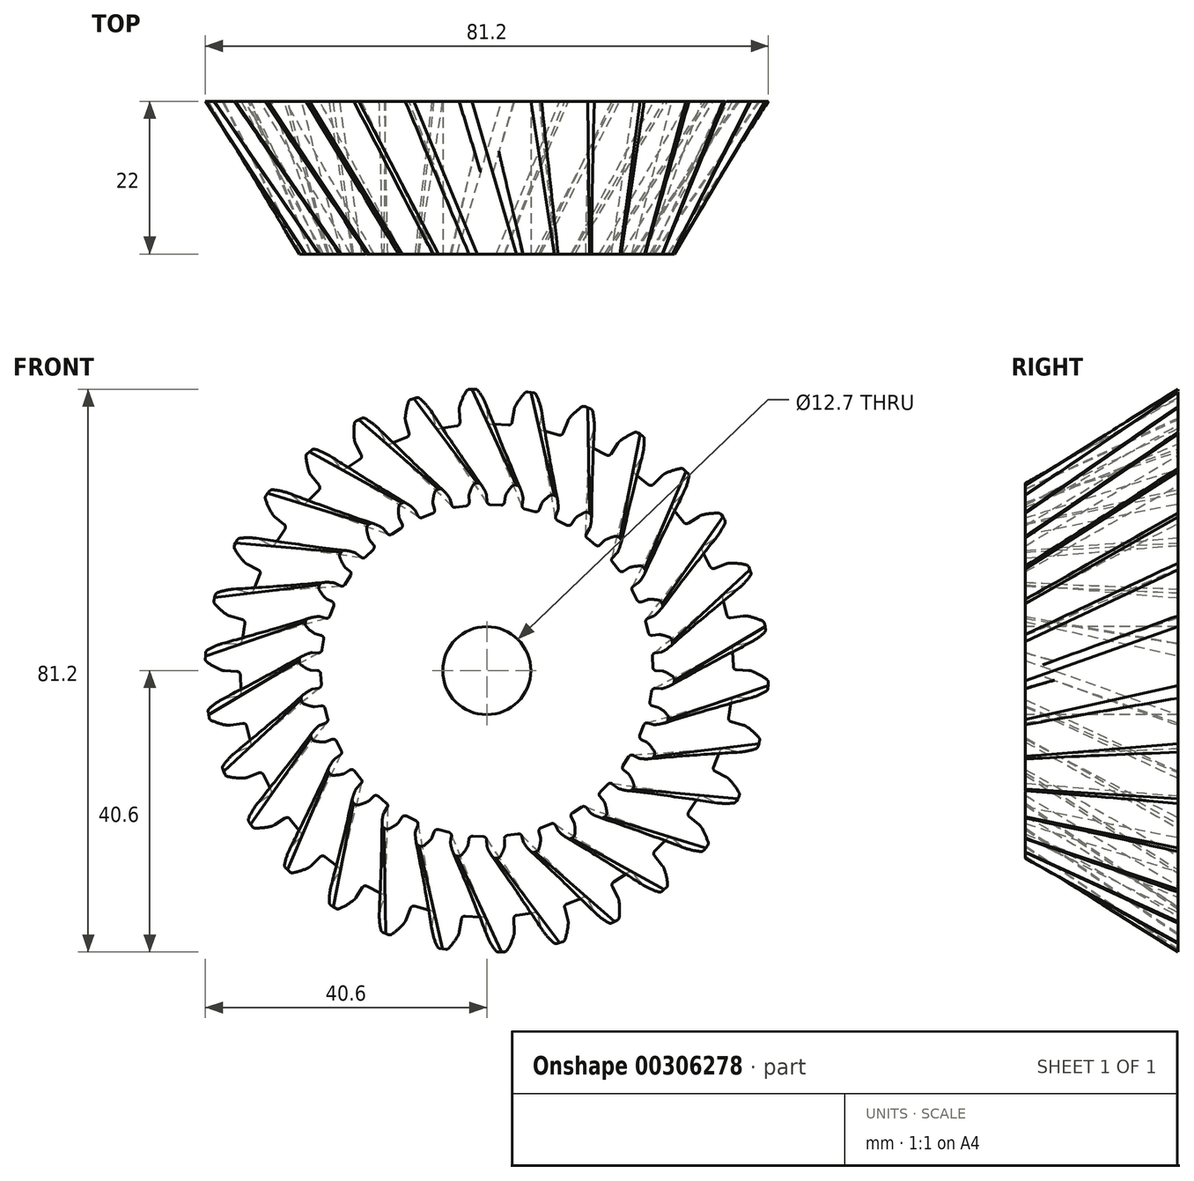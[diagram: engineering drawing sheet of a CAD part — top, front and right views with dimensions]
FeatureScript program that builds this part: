
annotation { "Feature Type Name" : "Feature", "Feature Type Description" : "" }
export const myFeature = defineFeature(function(context is Context, id is Id, definition is map)
    precondition{}
    {
        {
            var Q0;
            Q0=qCreatedBy(makeId("Front.planeOp"),FACE);
            var sketch = newSketch(context, id + "F0", { "sketchPlane" : qUnion([Q0])});
            skArc(sketch, "E0", {"start": v(-0.07, 25.48) * mm, "mid": v(-0.4, 26.19) * mm, "end": v(-0.83, 26.85) * mm});
            skLineSegment(sketch, "E1", {"start": v(-1.24, 27.06) * mm, "end": v(-1.82, 27.06) * mm});
            skLineSegment(sketch, "E2", {"start": v(-0.04, 25.32) * mm, "end": v(0, 24.44) * mm});
            skArc(sketch, "E3.MirrorCS", {"start": v(-2.56, 25.38) * mm, "mid": v(-2.3, 26.1) * mm, "end": v(-1.97, 26.78) * mm});
            skLineSegment(sketch, "E4.MirrorCS", {"start": v(-1.58, 27.03) * mm, "end": v(-0.9, 27.1) * mm});
            skLineSegment(sketch, "E5.MirrorCS", {"start": v(-2.58, 25.21) * mm, "end": v(-2.54, 24.3) * mm});
            skPoint(sketch, "E6.visualSharp", {"position": v(-2.5, 23.57) * mm});
            skArc(sketch, "E6.filletArc", {"start": v(-2.97, 23.78) * mm, "mid": v(-2.65, 23.96) * mm, "end": v(-2.54, 24.3) * mm});
            skPoint(sketch, "E7.visualSharp", {"position": v(0.05, 23.7) * mm});
            skArc(sketch, "E7.filletArc", {"start": v(0, 24.44) * mm, "mid": v(0.16, 24.1) * mm, "end": v(0.5, 23.96) * mm});
            skPoint(sketch, "E8.visualSharp", {"position": v(-2.59, 25.3) * mm});
            skArc(sketch, "E8.filletArc", {"start": v(-2.56, 25.38) * mm, "mid": v(-2.58, 25.3) * mm, "end": v(-2.58, 25.21) * mm});
            skPoint(sketch, "E9.visualSharp", {"position": v(-0.04, 25.4) * mm});
            skArc(sketch, "E9.filletArc", {"start": v(-0.04, 25.32) * mm, "mid": v(-0.05, 25.4) * mm, "end": v(-0.07, 25.48) * mm});
            skPoint(sketch, "E10.visualSharp", {"position": v(-0.99, 27.06) * mm});
            skArc(sketch, "E10.filletArc", {"start": v(-0.83, 26.85) * mm, "mid": v(-1, 27) * mm, "end": v(-1.24, 27.06) * mm});
            skPoint(sketch, "E11.visualSharp", {"position": v(-1.83, 27) * mm});
            skArc(sketch, "E11.filletArc", {"start": v(-1.58, 27.03) * mm, "mid": v(-1.8, 26.95) * mm, "end": v(-1.97, 26.78) * mm});
            skPoint(sketch, "E12.1.0", {"position": v(-6.6, 26.26) * mm});
            skLineSegment(sketch, "E12.1.1", {"start": v(-5.3, 24.75) * mm, "end": v(-5.07, 23.9) * mm});
            skArc(sketch, "E12.1.2", {"start": v(-5.07, 23.9) * mm, "mid": v(-4.85, 23.6) * mm, "end": v(-4.5, 23.54) * mm});
            skPoint(sketch, "E12.1.3", {"position": v(-4.88, 23.2) * mm});
            skArc(sketch, "E12.1.4", {"start": v(-7.78, 24.29) * mm, "mid": v(-7.69, 25.05) * mm, "end": v(-7.5, 25.78) * mm});
            skArc(sketch, "E12.1.5", {"start": v(-7.85, 22.64) * mm, "mid": v(-7.57, 22.88) * mm, "end": v(-7.53, 23.25) * mm});
            skLineSegment(sketch, "E12.1.6", {"start": v(-7.77, 24.12) * mm, "end": v(-7.53, 23.25) * mm});
            skArc(sketch, "E12.1.7", {"start": v(-5.37, 24.9) * mm, "mid": v(-5.84, 25.53) * mm, "end": v(-6.4, 26.09) * mm});
            skPoint(sketch, "E12.1.8", {"position": v(-7.34, 22.54) * mm});
            skPoint(sketch, "E12.1.9", {"position": v(-5.32, 24.83) * mm});
            skPoint(sketch, "E12.1.10", {"position": v(-7.79, 24.2) * mm});
            skPoint(sketch, "E12.1.11", {"position": v(-7.4, 26.03) * mm});
            skArc(sketch, "E12.1.12", {"start": v(-7.17, 26.11) * mm, "mid": v(-7.37, 25.99) * mm, "end": v(-7.5, 25.78) * mm});
            skArc(sketch, "E12.1.13", {"start": v(-6.4, 26.09) * mm, "mid": v(-6.6, 26.2) * mm, "end": v(-6.84, 26.2) * mm});
            skArc(sketch, "E12.1.14", {"start": v(-5.3, 24.75) * mm, "mid": v(-5.33, 24.83) * mm, "end": v(-5.37, 24.9) * mm});
            skArc(sketch, "E12.1.15", {"start": v(-7.78, 24.29) * mm, "mid": v(-7.78, 24.2) * mm, "end": v(-7.77, 24.12) * mm});
            skLineSegment(sketch, "E12.1.16", {"start": v(-6.84, 26.2) * mm, "end": v(-7.4, 26.09) * mm});
            skLineSegment(sketch, "E12.1.17", {"start": v(-7.17, 26.11) * mm, "end": v(-6.52, 26.32) * mm});
            skPoint(sketch, "E12.2.0", {"position": v(-11.9, 24.31) * mm});
            skLineSegment(sketch, "E12.2.1", {"start": v(-10.33, 23.11) * mm, "end": v(-9.93, 22.33) * mm});
            skArc(sketch, "E12.2.2", {"start": v(-9.93, 22.33) * mm, "mid": v(-9.66, 22.08) * mm, "end": v(-9.29, 22.09) * mm});
            skPoint(sketch, "E12.2.3", {"position": v(-9.6, 21.67) * mm});
            skArc(sketch, "E12.2.4", {"start": v(-12.66, 22.14) * mm, "mid": v(-12.72, 22.9) * mm, "end": v(-12.7, 23.66) * mm});
            skArc(sketch, "E12.2.5", {"start": v(-12.39, 20.51) * mm, "mid": v(-12.17, 20.8) * mm, "end": v(-12.2, 21.17) * mm});
            skLineSegment(sketch, "E12.2.6", {"start": v(-12.61, 21.98) * mm, "end": v(-12.2, 21.17) * mm});
            skArc(sketch, "E12.2.7", {"start": v(-10.43, 23.24) * mm, "mid": v(-11.02, 23.76) * mm, "end": v(-11.68, 24.19) * mm});
            skPoint(sketch, "E12.2.8", {"position": v(-11.87, 20.52) * mm});
            skPoint(sketch, "E12.2.9", {"position": v(-10.37, 23.18) * mm});
            skPoint(sketch, "E12.2.10", {"position": v(-12.65, 22.05) * mm});
            skPoint(sketch, "E12.2.11", {"position": v(-12.66, 23.92) * mm});
            skArc(sketch, "E12.2.12", {"start": v(-12.44, 24.05) * mm, "mid": v(-12.61, 23.89) * mm, "end": v(-12.7, 23.66) * mm});
            skArc(sketch, "E12.2.13", {"start": v(-11.68, 24.19) * mm, "mid": v(-11.9, 24.26) * mm, "end": v(-12.14, 24.21) * mm});
            skArc(sketch, "E12.2.14", {"start": v(-10.33, 23.11) * mm, "mid": v(-10.37, 23.18) * mm, "end": v(-10.43, 23.24) * mm});
            skArc(sketch, "E12.2.15", {"start": v(-12.66, 22.14) * mm, "mid": v(-12.65, 22.06) * mm, "end": v(-12.61, 21.98) * mm});
            skLineSegment(sketch, "E12.2.16", {"start": v(-12.14, 24.21) * mm, "end": v(-12.67, 23.98) * mm});
            skLineSegment(sketch, "E12.2.17", {"start": v(-12.44, 24.05) * mm, "end": v(-11.85, 24.4) * mm});
            skPoint(sketch, "E12.3.0", {"position": v(-16.7, 21.3) * mm});
            skLineSegment(sketch, "E12.3.1", {"start": v(-14.91, 20.46) * mm, "end": v(-14.36, 19.77) * mm});
            skArc(sketch, "E12.3.2", {"start": v(-14.36, 19.77) * mm, "mid": v(-14.04, 19.6) * mm, "end": v(-13.68, 19.67) * mm});
            skPoint(sketch, "E12.3.3", {"position": v(-13.9, 19.2) * mm});
            skArc(sketch, "E12.3.4", {"start": v(-17, 19.02) * mm, "mid": v(-17.2, 19.75) * mm, "end": v(-17.33, 20.5) * mm});
            skArc(sketch, "E12.3.5", {"start": v(-16.38, 17.49) * mm, "mid": v(-16.23, 17.82) * mm, "end": v(-16.34, 18.17) * mm});
            skLineSegment(sketch, "E12.3.6", {"start": v(-16.9, 18.88) * mm, "end": v(-16.34, 18.17) * mm});
            skArc(sketch, "E12.3.7", {"start": v(-15.03, 20.57) * mm, "mid": v(-15.72, 20.94) * mm, "end": v(-16.45, 21.23) * mm});
            skPoint(sketch, "E12.3.8", {"position": v(-15.88, 17.6) * mm});
            skPoint(sketch, "E12.3.9", {"position": v(-14.96, 20.52) * mm});
            skPoint(sketch, "E12.3.10", {"position": v(-16.96, 18.94) * mm});
            skPoint(sketch, "E12.3.11", {"position": v(-17.36, 20.77) * mm});
            skArc(sketch, "E12.3.12", {"start": v(-17.17, 20.94) * mm, "mid": v(-17.3, 20.74) * mm, "end": v(-17.33, 20.5) * mm});
            skArc(sketch, "E12.3.13", {"start": v(-16.45, 21.23) * mm, "mid": v(-16.69, 21.25) * mm, "end": v(-16.9, 21.16) * mm});
            skArc(sketch, "E12.3.14", {"start": v(-14.91, 20.46) * mm, "mid": v(-14.97, 20.52) * mm, "end": v(-15.03, 20.57) * mm});
            skArc(sketch, "E12.3.15", {"start": v(-17, 19.02) * mm, "mid": v(-16.96, 18.95) * mm, "end": v(-16.9, 18.88) * mm});
            skLineSegment(sketch, "E12.3.16", {"start": v(-16.9, 21.16) * mm, "end": v(-17.38, 20.82) * mm});
            skLineSegment(sketch, "E12.3.17", {"start": v(-17.17, 20.94) * mm, "end": v(-16.66, 21.4) * mm});
            skPoint(sketch, "E12.4.0", {"position": v(-20.77, 17.37) * mm});
            skLineSegment(sketch, "E12.4.1", {"start": v(-18.84, 16.91) * mm, "end": v(-18.15, 16.36) * mm});
            skArc(sketch, "E12.4.2", {"start": v(-18.15, 16.36) * mm, "mid": v(-17.8, 16.25) * mm, "end": v(-17.47, 16.4) * mm});
            skPoint(sketch, "E12.4.3", {"position": v(-17.58, 15.9) * mm});
            skArc(sketch, "E12.4.4", {"start": v(-20.57, 15.08) * mm, "mid": v(-20.94, 15.75) * mm, "end": v(-21.22, 16.45) * mm});
            skArc(sketch, "E12.4.5", {"start": v(-19.66, 13.7) * mm, "mid": v(-19.58, 14.06) * mm, "end": v(-19.76, 14.38) * mm});
            skLineSegment(sketch, "E12.4.6", {"start": v(-20.46, 14.95) * mm, "end": v(-19.76, 14.38) * mm});
            skArc(sketch, "E12.4.7", {"start": v(-18.98, 17) * mm, "mid": v(-19.73, 17.22) * mm, "end": v(-20.5, 17.35) * mm});
            skPoint(sketch, "E12.4.8", {"position": v(-19.2, 13.92) * mm});
            skPoint(sketch, "E12.4.9", {"position": v(-18.9, 16.96) * mm});
            skPoint(sketch, "E12.4.10", {"position": v(-20.53, 15) * mm});
            skPoint(sketch, "E12.4.11", {"position": v(-21.3, 16.7) * mm});
            skArc(sketch, "E12.4.12", {"start": v(-21.15, 16.91) * mm, "mid": v(-21.24, 16.7) * mm, "end": v(-21.22, 16.45) * mm});
            skArc(sketch, "E12.4.13", {"start": v(-20.5, 17.35) * mm, "mid": v(-20.74, 17.32) * mm, "end": v(-20.94, 17.18) * mm});
            skArc(sketch, "E12.4.14", {"start": v(-18.84, 16.91) * mm, "mid": v(-18.9, 16.96) * mm, "end": v(-18.98, 17) * mm});
            skArc(sketch, "E12.4.15", {"start": v(-20.57, 15.08) * mm, "mid": v(-20.52, 15) * mm, "end": v(-20.46, 14.95) * mm});
            skLineSegment(sketch, "E12.4.16", {"start": v(-20.94, 17.18) * mm, "end": v(-21.33, 16.75) * mm});
            skLineSegment(sketch, "E12.4.17", {"start": v(-21.15, 16.91) * mm, "end": v(-20.75, 17.46) * mm});
            skPoint(sketch, "E12.5.0", {"position": v(-23.93, 12.67) * mm});
            skLineSegment(sketch, "E12.5.1", {"start": v(-21.94, 12.62) * mm, "end": v(-21.16, 12.23) * mm});
            skArc(sketch, "E12.5.2", {"start": v(-21.16, 12.23) * mm, "mid": v(-20.8, 12.19) * mm, "end": v(-20.5, 12.4) * mm});
            skPoint(sketch, "E12.5.3", {"position": v(-20.5, 11.9) * mm});
            skArc(sketch, "E12.5.4", {"start": v(-23.26, 10.47) * mm, "mid": v(-23.75, 11.05) * mm, "end": v(-24.18, 11.68) * mm});
            skArc(sketch, "E12.5.5", {"start": v(-22.08, 9.31) * mm, "mid": v(-22.07, 9.68) * mm, "end": v(-22.32, 9.96) * mm});
            skLineSegment(sketch, "E12.5.6", {"start": v(-23.12, 10.37) * mm, "end": v(-22.32, 9.96) * mm});
            skArc(sketch, "E12.5.7", {"start": v(-22.1, 12.68) * mm, "mid": v(-22.88, 12.74) * mm, "end": v(-23.66, 12.7) * mm});
            skPoint(sketch, "E12.5.8", {"position": v(-21.67, 9.62) * mm});
            skPoint(sketch, "E12.5.9", {"position": v(-22.02, 12.66) * mm});
            skPoint(sketch, "E12.5.10", {"position": v(-23.2, 10.4) * mm});
            skPoint(sketch, "E12.5.11", {"position": v(-24.3, 11.91) * mm});
            skArc(sketch, "E12.5.12", {"start": v(-24.2, 12.14) * mm, "mid": v(-24.24, 11.91) * mm, "end": v(-24.18, 11.68) * mm});
            skArc(sketch, "E12.5.13", {"start": v(-23.66, 12.7) * mm, "mid": v(-23.89, 12.63) * mm, "end": v(-24.05, 12.45) * mm});
            skArc(sketch, "E12.5.14", {"start": v(-21.94, 12.62) * mm, "mid": v(-22.02, 12.66) * mm, "end": v(-22.1, 12.68) * mm});
            skArc(sketch, "E12.5.15", {"start": v(-23.26, 10.47) * mm, "mid": v(-23.2, 10.41) * mm, "end": v(-23.12, 10.37) * mm});
            skLineSegment(sketch, "E12.5.16", {"start": v(-24.05, 12.45) * mm, "end": v(-24.34, 11.95) * mm});
            skLineSegment(sketch, "E12.5.17", {"start": v(-24.2, 12.14) * mm, "end": v(-23.93, 12.77) * mm});
            skPoint(sketch, "E12.6.0", {"position": v(-26.04, 7.42) * mm});
            skLineSegment(sketch, "E12.6.1", {"start": v(-24.09, 7.79) * mm, "end": v(-23.24, 7.56) * mm});
            skArc(sketch, "E12.6.2", {"start": v(-23.24, 7.56) * mm, "mid": v(-22.87, 7.6) * mm, "end": v(-22.63, 7.88) * mm});
            skPoint(sketch, "E12.6.3", {"position": v(-22.53, 7.37) * mm});
            skArc(sketch, "E12.6.4", {"start": v(-24.93, 5.4) * mm, "mid": v(-25.53, 5.87) * mm, "end": v(-26.08, 6.4) * mm});
            skArc(sketch, "E12.6.5", {"start": v(-23.53, 4.52) * mm, "mid": v(-23.6, 4.88) * mm, "end": v(-23.9, 5.1) * mm});
            skLineSegment(sketch, "E12.6.6", {"start": v(-24.77, 5.33) * mm, "end": v(-23.9, 5.1) * mm});
            skArc(sketch, "E12.6.7", {"start": v(-24.25, 7.8) * mm, "mid": v(-25.03, 7.7) * mm, "end": v(-25.79, 7.5) * mm});
            skPoint(sketch, "E12.6.8", {"position": v(-23.2, 4.9) * mm});
            skPoint(sketch, "E12.6.9", {"position": v(-24.17, 7.8) * mm});
            skPoint(sketch, "E12.6.10", {"position": v(-24.86, 5.36) * mm});
            skPoint(sketch, "E12.6.11", {"position": v(-26.25, 6.6) * mm});
            skArc(sketch, "E12.6.12", {"start": v(-26.2, 6.85) * mm, "mid": v(-26.2, 6.6) * mm, "end": v(-26.08, 6.4) * mm});
            skArc(sketch, "E12.6.13", {"start": v(-25.79, 7.5) * mm, "mid": v(-26, 7.38) * mm, "end": v(-26.11, 7.18) * mm});
            skArc(sketch, "E12.6.14", {"start": v(-24.09, 7.79) * mm, "mid": v(-24.17, 7.8) * mm, "end": v(-24.25, 7.8) * mm});
            skArc(sketch, "E12.6.15", {"start": v(-24.93, 5.4) * mm, "mid": v(-24.85, 5.36) * mm, "end": v(-24.77, 5.33) * mm});
            skLineSegment(sketch, "E12.6.16", {"start": v(-26.11, 7.18) * mm, "end": v(-26.3, 6.63) * mm});
            skLineSegment(sketch, "E12.6.17", {"start": v(-26.2, 6.85) * mm, "end": v(-26.06, 7.51) * mm});
            skPoint(sketch, "E12.7.0", {"position": v(-27.01, 1.85) * mm});
            skLineSegment(sketch, "E12.7.1", {"start": v(-25.18, 2.6) * mm, "end": v(-24.3, 2.56) * mm});
            skArc(sketch, "E12.7.2", {"start": v(-24.3, 2.56) * mm, "mid": v(-23.95, 2.68) * mm, "end": v(-23.77, 3) * mm});
            skPoint(sketch, "E12.7.3", {"position": v(-23.57, 2.52) * mm});
            skArc(sketch, "E12.7.4", {"start": v(-25.5, 0.1) * mm, "mid": v(-26.2, 0.43) * mm, "end": v(-26.84, 0.84) * mm});
            skArc(sketch, "E12.7.5", {"start": v(-23.96, -0.47) * mm, "mid": v(-24.1, -0.13) * mm, "end": v(-24.44, 0.02) * mm});
            skLineSegment(sketch, "E12.7.6", {"start": v(-25.34, 0.07) * mm, "end": v(-24.44, 0.02) * mm});
            skArc(sketch, "E12.7.7", {"start": v(-25.35, 2.6) * mm, "mid": v(-26.08, 2.33) * mm, "end": v(-26.79, 1.98) * mm});
            skPoint(sketch, "E12.7.8", {"position": v(-23.7, -0.02) * mm});
            skPoint(sketch, "E12.7.9", {"position": v(-25.26, 2.61) * mm});
            skPoint(sketch, "E12.7.10", {"position": v(-25.43, 0.07) * mm});
            skPoint(sketch, "E12.7.11", {"position": v(-27.05, 1) * mm});
            skArc(sketch, "E12.7.12", {"start": v(-27.05, 1.25) * mm, "mid": v(-27, 1.02) * mm, "end": v(-26.84, 0.84) * mm});
            skArc(sketch, "E12.7.13", {"start": v(-26.79, 1.98) * mm, "mid": v(-26.96, 1.82) * mm, "end": v(-27.04, 1.6) * mm});
            skArc(sketch, "E12.7.14", {"start": v(-25.18, 2.6) * mm, "mid": v(-25.26, 2.6) * mm, "end": v(-25.35, 2.6) * mm});
            skArc(sketch, "E12.7.15", {"start": v(-25.5, 0.1) * mm, "mid": v(-25.43, 0.08) * mm, "end": v(-25.34, 0.07) * mm});
            skLineSegment(sketch, "E12.7.16", {"start": v(-27.04, 1.6) * mm, "end": v(-27.1, 1.02) * mm});
            skLineSegment(sketch, "E12.7.17", {"start": v(-27.05, 1.25) * mm, "end": v(-27.05, 1.93) * mm});
            skPoint(sketch, "E12.8.0", {"position": v(-26.8, -3.81) * mm});
            skLineSegment(sketch, "E12.8.1", {"start": v(-25.17, -2.68) * mm, "end": v(-24.3, -2.55) * mm});
            skArc(sketch, "E12.8.2", {"start": v(-24.3, -2.55) * mm, "mid": v(-23.99, -2.36) * mm, "end": v(-23.88, -2) * mm});
            skPoint(sketch, "E12.8.3", {"position": v(-23.58, -2.43) * mm});
            skArc(sketch, "E12.8.4", {"start": v(-24.97, -5.2) * mm, "mid": v(-25.71, -5.03) * mm, "end": v(-26.43, -4.76) * mm});
            skArc(sketch, "E12.8.5", {"start": v(-23.34, -5.44) * mm, "mid": v(-23.55, -5.14) * mm, "end": v(-23.9, -5.06) * mm});
            skLineSegment(sketch, "E12.8.6", {"start": v(-24.8, -5.2) * mm, "end": v(-23.9, -5.06) * mm});
            skArc(sketch, "E12.8.7", {"start": v(-25.33, -2.74) * mm, "mid": v(-26, -3.14) * mm, "end": v(-26.61, -3.63) * mm});
            skPoint(sketch, "E12.8.8", {"position": v(-23.18, -4.95) * mm});
            skPoint(sketch, "E12.8.9", {"position": v(-25.25, -2.7) * mm});
            skPoint(sketch, "E12.8.10", {"position": v(-24.88, -5.22) * mm});
            skPoint(sketch, "E12.8.11", {"position": v(-26.67, -4.65) * mm});
            skArc(sketch, "E12.8.12", {"start": v(-26.72, -4.4) * mm, "mid": v(-26.62, -4.61) * mm, "end": v(-26.43, -4.76) * mm});
            skArc(sketch, "E12.8.13", {"start": v(-26.61, -3.63) * mm, "mid": v(-26.75, -3.83) * mm, "end": v(-26.78, -4.06) * mm});
            skArc(sketch, "E12.8.14", {"start": v(-25.17, -2.68) * mm, "mid": v(-25.25, -2.7) * mm, "end": v(-25.33, -2.74) * mm});
            skArc(sketch, "E12.8.15", {"start": v(-24.97, -5.2) * mm, "mid": v(-24.89, -5.21) * mm, "end": v(-24.8, -5.2) * mm});
            skLineSegment(sketch, "E12.8.16", {"start": v(-26.78, -4.06) * mm, "end": v(-26.72, -4.64) * mm});
            skLineSegment(sketch, "E12.8.17", {"start": v(-26.72, -4.4) * mm, "end": v(-26.86, -3.74) * mm});
            skPoint(sketch, "E12.9.0", {"position": v(-25.43, -9.3) * mm});
            skLineSegment(sketch, "E12.9.1", {"start": v(-24.06, -7.86) * mm, "end": v(-23.24, -7.54) * mm});
            skArc(sketch, "E12.9.2", {"start": v(-23.24, -7.54) * mm, "mid": v(-22.97, -7.3) * mm, "end": v(-22.94, -6.93) * mm});
            skPoint(sketch, "E12.9.3", {"position": v(-22.56, -7.28) * mm});
            skArc(sketch, "E12.9.4", {"start": v(-23.34, -10.28) * mm, "mid": v(-24.1, -10.26) * mm, "end": v(-24.86, -10.15) * mm});
            skArc(sketch, "E12.9.5", {"start": v(-21.7, -10.17) * mm, "mid": v(-21.97, -9.92) * mm, "end": v(-22.33, -9.92) * mm});
            skLineSegment(sketch, "E12.9.6", {"start": v(-23.18, -10.25) * mm, "end": v(-22.33, -9.92) * mm});
            skArc(sketch, "E12.9.7", {"start": v(-24.2, -7.94) * mm, "mid": v(-24.78, -8.48) * mm, "end": v(-25.28, -9.08) * mm});
            skPoint(sketch, "E12.9.8", {"position": v(-21.65, -9.66) * mm});
            skPoint(sketch, "E12.9.9", {"position": v(-24.14, -7.89) * mm});
            skPoint(sketch, "E12.9.10", {"position": v(-23.26, -10.28) * mm});
            skPoint(sketch, "E12.9.11", {"position": v(-25.12, -10.1) * mm});
            skArc(sketch, "E12.9.12", {"start": v(-25.22, -9.86) * mm, "mid": v(-25.07, -10.05) * mm, "end": v(-24.86, -10.15) * mm});
            skArc(sketch, "E12.9.13", {"start": v(-25.28, -9.08) * mm, "mid": v(-25.37, -9.3) * mm, "end": v(-25.35, -9.54) * mm});
            skArc(sketch, "E12.9.14", {"start": v(-24.06, -7.86) * mm, "mid": v(-24.14, -7.9) * mm, "end": v(-24.2, -7.94) * mm});
            skArc(sketch, "E12.9.15", {"start": v(-23.34, -10.28) * mm, "mid": v(-23.26, -10.27) * mm, "end": v(-23.18, -10.25) * mm});
            skLineSegment(sketch, "E12.9.16", {"start": v(-25.35, -9.54) * mm, "end": v(-25.17, -10.1) * mm});
            skLineSegment(sketch, "E12.9.17", {"start": v(-25.22, -9.86) * mm, "end": v(-25.5, -9.24) * mm});
            skPoint(sketch, "E12.10.0", {"position": v(-22.94, -14.38) * mm});
            skLineSegment(sketch, "E12.10.1", {"start": v(-21.9, -12.7) * mm, "end": v(-21.17, -12.21) * mm});
            skArc(sketch, "E12.10.2", {"start": v(-21.17, -12.21) * mm, "mid": v(-20.95, -11.91) * mm, "end": v(-21, -11.55) * mm});
            skPoint(sketch, "E12.10.3", {"position": v(-20.55, -11.81) * mm});
            skArc(sketch, "E12.10.4", {"start": v(-20.7, -14.9) * mm, "mid": v(-21.45, -15.05) * mm, "end": v(-22.2, -15.1) * mm});
            skArc(sketch, "E12.10.5", {"start": v(-19.1, -14.46) * mm, "mid": v(-19.42, -14.27) * mm, "end": v(-19.78, -14.35) * mm});
            skLineSegment(sketch, "E12.10.6", {"start": v(-20.54, -14.84) * mm, "end": v(-19.78, -14.35) * mm});
            skArc(sketch, "E12.10.7", {"start": v(-22.03, -12.8) * mm, "mid": v(-22.47, -13.45) * mm, "end": v(-22.83, -14.14) * mm});
            skPoint(sketch, "E12.10.8", {"position": v(-19.17, -13.95) * mm});
            skPoint(sketch, "E12.10.9", {"position": v(-21.97, -12.74) * mm});
            skPoint(sketch, "E12.10.10", {"position": v(-20.61, -14.89) * mm});
            skPoint(sketch, "E12.10.11", {"position": v(-22.47, -15.1) * mm});
            skArc(sketch, "E12.10.12", {"start": v(-22.62, -14.89) * mm, "mid": v(-22.44, -15.04) * mm, "end": v(-22.2, -15.1) * mm});
            skArc(sketch, "E12.10.13", {"start": v(-22.83, -14.14) * mm, "mid": v(-22.88, -14.37) * mm, "end": v(-22.81, -14.6) * mm});
            skArc(sketch, "E12.10.14", {"start": v(-21.9, -12.7) * mm, "mid": v(-21.97, -12.74) * mm, "end": v(-22.03, -12.8) * mm});
            skArc(sketch, "E12.10.15", {"start": v(-20.7, -14.9) * mm, "mid": v(-20.62, -14.88) * mm, "end": v(-20.54, -14.84) * mm});
            skLineSegment(sketch, "E12.10.16", {"start": v(-22.81, -14.6) * mm, "end": v(-22.52, -15.1) * mm});
            skLineSegment(sketch, "E12.10.17", {"start": v(-22.62, -14.89) * mm, "end": v(-23.02, -14.34) * mm});
            skPoint(sketch, "E12.11.0", {"position": v(-19.44, -18.84) * mm});
            skLineSegment(sketch, "E12.11.1", {"start": v(-18.79, -16.97) * mm, "end": v(-18.17, -16.34) * mm});
            skArc(sketch, "E12.11.2", {"start": v(-18.17, -16.34) * mm, "mid": v(-18.02, -16) * mm, "end": v(-18.14, -15.66) * mm});
            skPoint(sketch, "E12.11.3", {"position": v(-17.65, -15.83) * mm});
            skArc(sketch, "E12.11.4", {"start": v(-17.14, -18.89) * mm, "mid": v(-17.85, -19.18) * mm, "end": v(-18.58, -19.38) * mm});
            skArc(sketch, "E12.11.5", {"start": v(-15.68, -18.12) * mm, "mid": v(-16.03, -18) * mm, "end": v(-16.37, -18.15) * mm});
            skLineSegment(sketch, "E12.11.6", {"start": v(-17, -18.79) * mm, "end": v(-16.37, -18.15) * mm});
            skArc(sketch, "E12.11.7", {"start": v(-18.88, -17.1) * mm, "mid": v(-19.19, -17.83) * mm, "end": v(-19.4, -18.58) * mm});
            skPoint(sketch, "E12.11.8", {"position": v(-15.85, -17.63) * mm});
            skPoint(sketch, "E12.11.9", {"position": v(-18.85, -17.03) * mm});
            skPoint(sketch, "E12.11.10", {"position": v(-17.07, -18.85) * mm});
            skPoint(sketch, "E12.11.11", {"position": v(-18.84, -19.43) * mm});
            skArc(sketch, "E12.11.12", {"start": v(-19.03, -19.26) * mm, "mid": v(-18.82, -19.38) * mm, "end": v(-18.58, -19.38) * mm});
            skArc(sketch, "E12.11.13", {"start": v(-19.4, -18.58) * mm, "mid": v(-19.39, -18.82) * mm, "end": v(-19.28, -19.03) * mm});
            skArc(sketch, "E12.11.14", {"start": v(-18.79, -16.97) * mm, "mid": v(-18.84, -17.03) * mm, "end": v(-18.88, -17.1) * mm});
            skArc(sketch, "E12.11.15", {"start": v(-17.14, -18.89) * mm, "mid": v(-17.07, -18.84) * mm, "end": v(-17, -18.79) * mm});
            skLineSegment(sketch, "E12.11.16", {"start": v(-19.28, -19.03) * mm, "end": v(-18.89, -19.46) * mm});
            skLineSegment(sketch, "E12.11.17", {"start": v(-19.03, -19.26) * mm, "end": v(-19.53, -18.8) * mm});
            skPoint(sketch, "E12.12.0", {"position": v(-15.1, -22.47) * mm});
            skLineSegment(sketch, "E12.12.1", {"start": v(-14.85, -20.5) * mm, "end": v(-14.37, -19.76) * mm});
            skArc(sketch, "E12.12.2", {"start": v(-14.37, -19.76) * mm, "mid": v(-14.3, -19.4) * mm, "end": v(-14.48, -19.09) * mm});
            skPoint(sketch, "E12.12.3", {"position": v(-13.97, -19.15) * mm});
            skArc(sketch, "E12.12.4", {"start": v(-12.84, -22.04) * mm, "mid": v(-13.47, -22.47) * mm, "end": v(-14.15, -22.82) * mm});
            skArc(sketch, "E12.12.5", {"start": v(-11.57, -20.98) * mm, "mid": v(-11.94, -20.94) * mm, "end": v(-12.24, -21.16) * mm});
            skLineSegment(sketch, "E12.12.6", {"start": v(-12.73, -21.91) * mm, "end": v(-12.24, -21.16) * mm});
            skArc(sketch, "E12.12.7", {"start": v(-14.92, -20.65) * mm, "mid": v(-15.06, -21.42) * mm, "end": v(-15.1, -22.2) * mm});
            skPoint(sketch, "E12.12.8", {"position": v(-11.84, -20.54) * mm});
            skPoint(sketch, "E12.12.9", {"position": v(-14.9, -20.57) * mm});
            skPoint(sketch, "E12.12.10", {"position": v(-12.77, -21.98) * mm});
            skPoint(sketch, "E12.12.11", {"position": v(-14.39, -22.93) * mm});
            skArc(sketch, "E12.12.12", {"start": v(-14.6, -22.8) * mm, "mid": v(-14.38, -22.87) * mm, "end": v(-14.15, -22.82) * mm});
            skArc(sketch, "E12.12.13", {"start": v(-15.1, -22.2) * mm, "mid": v(-15.05, -22.44) * mm, "end": v(-14.9, -22.62) * mm});
            skArc(sketch, "E12.12.14", {"start": v(-14.85, -20.5) * mm, "mid": v(-14.89, -20.58) * mm, "end": v(-14.92, -20.65) * mm});
            skArc(sketch, "E12.12.15", {"start": v(-12.84, -22.04) * mm, "mid": v(-12.78, -21.98) * mm, "end": v(-12.73, -21.91) * mm});
            skLineSegment(sketch, "E12.12.16", {"start": v(-14.9, -22.62) * mm, "end": v(-14.43, -22.96) * mm});
            skLineSegment(sketch, "E12.12.17", {"start": v(-14.6, -22.8) * mm, "end": v(-15.2, -22.46) * mm});
            skPoint(sketch, "E12.13.0", {"position": v(-10.1, -25.12) * mm});
            skLineSegment(sketch, "E12.13.1", {"start": v(-10.26, -23.14) * mm, "end": v(-9.95, -22.32) * mm});
            skArc(sketch, "E12.13.2", {"start": v(-9.95, -22.32) * mm, "mid": v(-9.95, -21.95) * mm, "end": v(-10.2, -21.68) * mm});
            skPoint(sketch, "E12.13.3", {"position": v(-9.68, -21.64) * mm});
            skArc(sketch, "E12.13.4", {"start": v(-7.98, -24.23) * mm, "mid": v(-8.5, -24.78) * mm, "end": v(-9.1, -25.27) * mm});
            skArc(sketch, "E12.13.5", {"start": v(-6.96, -22.93) * mm, "mid": v(-7.32, -22.96) * mm, "end": v(-7.57, -23.24) * mm});
            skLineSegment(sketch, "E12.13.6", {"start": v(-7.9, -24.08) * mm, "end": v(-7.57, -23.24) * mm});
            skArc(sketch, "E12.13.7", {"start": v(-10.3, -23.3) * mm, "mid": v(-10.28, -24.09) * mm, "end": v(-10.16, -24.86) * mm});
            skPoint(sketch, "E12.13.8", {"position": v(-7.3, -22.55) * mm});
            skPoint(sketch, "E12.13.9", {"position": v(-10.3, -23.22) * mm});
            skPoint(sketch, "E12.13.10", {"position": v(-7.92, -24.16) * mm});
            skPoint(sketch, "E12.13.11", {"position": v(-9.3, -25.42) * mm});
            skArc(sketch, "E12.13.12", {"start": v(-9.55, -25.34) * mm, "mid": v(-9.31, -25.36) * mm, "end": v(-9.1, -25.27) * mm});
            skArc(sketch, "E12.13.13", {"start": v(-10.16, -24.86) * mm, "mid": v(-10.06, -25.08) * mm, "end": v(-9.87, -25.22) * mm});
            skArc(sketch, "E12.13.14", {"start": v(-10.26, -23.14) * mm, "mid": v(-10.29, -23.22) * mm, "end": v(-10.3, -23.3) * mm});
            skArc(sketch, "E12.13.15", {"start": v(-7.98, -24.23) * mm, "mid": v(-7.93, -24.16) * mm, "end": v(-7.9, -24.08) * mm});
            skLineSegment(sketch, "E12.13.16", {"start": v(-9.87, -25.22) * mm, "end": v(-9.34, -25.46) * mm});
            skLineSegment(sketch, "E12.13.17", {"start": v(-9.55, -25.34) * mm, "end": v(-10.2, -25.13) * mm});
            skPoint(sketch, "E12.14.0", {"position": v(-4.66, -26.67) * mm});
            skLineSegment(sketch, "E12.14.1", {"start": v(-5.23, -24.77) * mm, "end": v(-5.09, -23.9) * mm});
            skArc(sketch, "E12.14.2", {"start": v(-5.09, -23.9) * mm, "mid": v(-5.17, -23.54) * mm, "end": v(-5.47, -23.33) * mm});
            skPoint(sketch, "E12.14.3", {"position": v(-4.97, -23.18) * mm});
            skArc(sketch, "E12.14.4", {"start": v(-2.77, -25.36) * mm, "mid": v(-3.17, -26) * mm, "end": v(-3.64, -26.6) * mm});
            skArc(sketch, "E12.14.5", {"start": v(-2.04, -23.88) * mm, "mid": v(-2.39, -23.98) * mm, "end": v(-2.57, -24.3) * mm});
            skLineSegment(sketch, "E12.14.6", {"start": v(-2.71, -25.2) * mm, "end": v(-2.57, -24.3) * mm});
            skArc(sketch, "E12.14.7", {"start": v(-5.23, -24.94) * mm, "mid": v(-5.04, -25.7) * mm, "end": v(-4.77, -26.43) * mm});
            skPoint(sketch, "E12.14.8", {"position": v(-2.46, -23.58) * mm});
            skPoint(sketch, "E12.14.9", {"position": v(-5.24, -24.85) * mm});
            skPoint(sketch, "E12.14.10", {"position": v(-2.73, -25.28) * mm});
            skPoint(sketch, "E12.14.11", {"position": v(-3.82, -26.8) * mm});
            skArc(sketch, "E12.14.12", {"start": v(-4.07, -26.77) * mm, "mid": v(-3.84, -26.74) * mm, "end": v(-3.64, -26.6) * mm});
            skArc(sketch, "E12.14.13", {"start": v(-4.77, -26.43) * mm, "mid": v(-4.63, -26.62) * mm, "end": v(-4.41, -26.72) * mm});
            skArc(sketch, "E12.14.14", {"start": v(-5.23, -24.77) * mm, "mid": v(-5.23, -24.85) * mm, "end": v(-5.23, -24.94) * mm});
            skArc(sketch, "E12.14.15", {"start": v(-2.77, -25.36) * mm, "mid": v(-2.73, -25.28) * mm, "end": v(-2.71, -25.2) * mm});
            skLineSegment(sketch, "E12.14.16", {"start": v(-4.41, -26.72) * mm, "end": v(-3.84, -26.84) * mm});
            skLineSegment(sketch, "E12.14.17", {"start": v(-4.07, -26.77) * mm, "end": v(-4.75, -26.7) * mm});
            skPoint(sketch, "E12.15.0", {"position": v(0.99, -27.06) * mm});
            skLineSegment(sketch, "E12.15.1", {"start": v(0.04, -25.32) * mm, "end": v(0, -24.44) * mm});
            skArc(sketch, "E12.15.2", {"start": v(0, -24.44) * mm, "mid": v(-0.16, -24.1) * mm, "end": v(-0.5, -23.96) * mm});
            skPoint(sketch, "E12.15.3", {"position": v(-0.05, -23.7) * mm});
            skArc(sketch, "E12.15.4", {"start": v(2.56, -25.38) * mm, "mid": v(2.3, -26.1) * mm, "end": v(1.97, -26.78) * mm});
            skArc(sketch, "E12.15.5", {"start": v(2.97, -23.78) * mm, "mid": v(2.65, -23.96) * mm, "end": v(2.54, -24.3) * mm});
            skLineSegment(sketch, "E12.15.6", {"start": v(2.58, -25.21) * mm, "end": v(2.54, -24.3) * mm});
            skArc(sketch, "E12.15.7", {"start": v(0.07, -25.48) * mm, "mid": v(0.4, -26.19) * mm, "end": v(0.83, -26.85) * mm});
            skPoint(sketch, "E12.15.8", {"position": v(2.5, -23.57) * mm});
            skPoint(sketch, "E12.15.9", {"position": v(0.04, -25.4) * mm});
            skPoint(sketch, "E12.15.10", {"position": v(2.59, -25.3) * mm});
            skPoint(sketch, "E12.15.11", {"position": v(1.83, -27) * mm});
            skArc(sketch, "E12.15.12", {"start": v(1.58, -27.03) * mm, "mid": v(1.8, -26.95) * mm, "end": v(1.97, -26.78) * mm});
            skArc(sketch, "E12.15.13", {"start": v(0.83, -26.85) * mm, "mid": v(1, -27) * mm, "end": v(1.24, -27.06) * mm});
            skArc(sketch, "E12.15.14", {"start": v(0.04, -25.32) * mm, "mid": v(0.05, -25.4) * mm, "end": v(0.07, -25.48) * mm});
            skArc(sketch, "E12.15.15", {"start": v(2.56, -25.38) * mm, "mid": v(2.58, -25.3) * mm, "end": v(2.58, -25.21) * mm});
            skLineSegment(sketch, "E12.15.16", {"start": v(1.24, -27.06) * mm, "end": v(1.82, -27.06) * mm});
            skLineSegment(sketch, "E12.15.17", {"start": v(1.58, -27.03) * mm, "end": v(0.9, -27.1) * mm});
            skPoint(sketch, "E12.16.0", {"position": v(6.6, -26.26) * mm});
            skLineSegment(sketch, "E12.16.1", {"start": v(5.3, -24.75) * mm, "end": v(5.07, -23.9) * mm});
            skArc(sketch, "E12.16.2", {"start": v(5.07, -23.9) * mm, "mid": v(4.85, -23.6) * mm, "end": v(4.5, -23.54) * mm});
            skPoint(sketch, "E12.16.3", {"position": v(4.88, -23.2) * mm});
            skArc(sketch, "E12.16.4", {"start": v(7.78, -24.29) * mm, "mid": v(7.69, -25.05) * mm, "end": v(7.5, -25.78) * mm});
            skArc(sketch, "E12.16.5", {"start": v(7.85, -22.64) * mm, "mid": v(7.57, -22.88) * mm, "end": v(7.53, -23.25) * mm});
            skLineSegment(sketch, "E12.16.6", {"start": v(7.77, -24.12) * mm, "end": v(7.53, -23.25) * mm});
            skArc(sketch, "E12.16.7", {"start": v(5.37, -24.9) * mm, "mid": v(5.84, -25.53) * mm, "end": v(6.4, -26.09) * mm});
            skPoint(sketch, "E12.16.8", {"position": v(7.34, -22.54) * mm});
            skPoint(sketch, "E12.16.9", {"position": v(5.32, -24.83) * mm});
            skPoint(sketch, "E12.16.10", {"position": v(7.79, -24.2) * mm});
            skPoint(sketch, "E12.16.11", {"position": v(7.4, -26.03) * mm});
            skArc(sketch, "E12.16.12", {"start": v(7.17, -26.11) * mm, "mid": v(7.37, -25.99) * mm, "end": v(7.5, -25.78) * mm});
            skArc(sketch, "E12.16.13", {"start": v(6.4, -26.09) * mm, "mid": v(6.6, -26.2) * mm, "end": v(6.84, -26.2) * mm});
            skArc(sketch, "E12.16.14", {"start": v(5.3, -24.75) * mm, "mid": v(5.33, -24.83) * mm, "end": v(5.37, -24.9) * mm});
            skArc(sketch, "E12.16.15", {"start": v(7.78, -24.29) * mm, "mid": v(7.78, -24.2) * mm, "end": v(7.77, -24.12) * mm});
            skLineSegment(sketch, "E12.16.16", {"start": v(6.84, -26.2) * mm, "end": v(7.4, -26.09) * mm});
            skLineSegment(sketch, "E12.16.17", {"start": v(7.17, -26.11) * mm, "end": v(6.52, -26.32) * mm});
            skPoint(sketch, "E12.17.0", {"position": v(11.9, -24.31) * mm});
            skLineSegment(sketch, "E12.17.1", {"start": v(10.33, -23.11) * mm, "end": v(9.93, -22.33) * mm});
            skArc(sketch, "E12.17.2", {"start": v(9.93, -22.33) * mm, "mid": v(9.66, -22.08) * mm, "end": v(9.29, -22.09) * mm});
            skPoint(sketch, "E12.17.3", {"position": v(9.6, -21.67) * mm});
            skArc(sketch, "E12.17.4", {"start": v(12.66, -22.14) * mm, "mid": v(12.72, -22.9) * mm, "end": v(12.7, -23.66) * mm});
            skArc(sketch, "E12.17.5", {"start": v(12.39, -20.51) * mm, "mid": v(12.17, -20.8) * mm, "end": v(12.2, -21.17) * mm});
            skLineSegment(sketch, "E12.17.6", {"start": v(12.61, -21.98) * mm, "end": v(12.2, -21.17) * mm});
            skArc(sketch, "E12.17.7", {"start": v(10.43, -23.24) * mm, "mid": v(11.02, -23.76) * mm, "end": v(11.68, -24.19) * mm});
            skPoint(sketch, "E12.17.8", {"position": v(11.87, -20.52) * mm});
            skPoint(sketch, "E12.17.9", {"position": v(10.37, -23.18) * mm});
            skPoint(sketch, "E12.17.10", {"position": v(12.65, -22.05) * mm});
            skPoint(sketch, "E12.17.11", {"position": v(12.66, -23.92) * mm});
            skArc(sketch, "E12.17.12", {"start": v(12.44, -24.05) * mm, "mid": v(12.61, -23.89) * mm, "end": v(12.7, -23.66) * mm});
            skArc(sketch, "E12.17.13", {"start": v(11.68, -24.19) * mm, "mid": v(11.9, -24.26) * mm, "end": v(12.14, -24.21) * mm});
            skArc(sketch, "E12.17.14", {"start": v(10.33, -23.11) * mm, "mid": v(10.37, -23.18) * mm, "end": v(10.43, -23.24) * mm});
            skArc(sketch, "E12.17.15", {"start": v(12.66, -22.14) * mm, "mid": v(12.65, -22.06) * mm, "end": v(12.61, -21.98) * mm});
            skLineSegment(sketch, "E12.17.16", {"start": v(12.14, -24.21) * mm, "end": v(12.67, -23.98) * mm});
            skLineSegment(sketch, "E12.17.17", {"start": v(12.44, -24.05) * mm, "end": v(11.85, -24.4) * mm});
            skPoint(sketch, "E12.18.0", {"position": v(16.7, -21.3) * mm});
            skLineSegment(sketch, "E12.18.1", {"start": v(14.91, -20.46) * mm, "end": v(14.36, -19.77) * mm});
            skArc(sketch, "E12.18.2", {"start": v(14.36, -19.77) * mm, "mid": v(14.04, -19.6) * mm, "end": v(13.68, -19.67) * mm});
            skPoint(sketch, "E12.18.3", {"position": v(13.9, -19.2) * mm});
            skArc(sketch, "E12.18.4", {"start": v(17, -19.02) * mm, "mid": v(17.2, -19.75) * mm, "end": v(17.33, -20.5) * mm});
            skArc(sketch, "E12.18.5", {"start": v(16.38, -17.49) * mm, "mid": v(16.23, -17.82) * mm, "end": v(16.34, -18.17) * mm});
            skLineSegment(sketch, "E12.18.6", {"start": v(16.9, -18.88) * mm, "end": v(16.34, -18.17) * mm});
            skArc(sketch, "E12.18.7", {"start": v(15.03, -20.57) * mm, "mid": v(15.72, -20.94) * mm, "end": v(16.45, -21.23) * mm});
            skPoint(sketch, "E12.18.8", {"position": v(15.88, -17.6) * mm});
            skPoint(sketch, "E12.18.9", {"position": v(14.96, -20.52) * mm});
            skPoint(sketch, "E12.18.10", {"position": v(16.96, -18.94) * mm});
            skPoint(sketch, "E12.18.11", {"position": v(17.36, -20.77) * mm});
            skArc(sketch, "E12.18.12", {"start": v(17.17, -20.94) * mm, "mid": v(17.3, -20.74) * mm, "end": v(17.33, -20.5) * mm});
            skArc(sketch, "E12.18.13", {"start": v(16.45, -21.23) * mm, "mid": v(16.69, -21.25) * mm, "end": v(16.9, -21.16) * mm});
            skArc(sketch, "E12.18.14", {"start": v(14.91, -20.46) * mm, "mid": v(14.97, -20.52) * mm, "end": v(15.03, -20.57) * mm});
            skArc(sketch, "E12.18.15", {"start": v(17, -19.02) * mm, "mid": v(16.96, -18.95) * mm, "end": v(16.9, -18.88) * mm});
            skLineSegment(sketch, "E12.18.16", {"start": v(16.9, -21.16) * mm, "end": v(17.38, -20.82) * mm});
            skLineSegment(sketch, "E12.18.17", {"start": v(17.17, -20.94) * mm, "end": v(16.66, -21.4) * mm});
            skPoint(sketch, "E12.19.0", {"position": v(20.77, -17.37) * mm});
            skLineSegment(sketch, "E12.19.1", {"start": v(18.84, -16.91) * mm, "end": v(18.15, -16.36) * mm});
            skArc(sketch, "E12.19.2", {"start": v(18.15, -16.36) * mm, "mid": v(17.8, -16.25) * mm, "end": v(17.47, -16.4) * mm});
            skPoint(sketch, "E12.19.3", {"position": v(17.58, -15.9) * mm});
            skArc(sketch, "E12.19.4", {"start": v(20.57, -15.08) * mm, "mid": v(20.94, -15.75) * mm, "end": v(21.22, -16.45) * mm});
            skArc(sketch, "E12.19.5", {"start": v(19.66, -13.7) * mm, "mid": v(19.58, -14.06) * mm, "end": v(19.76, -14.38) * mm});
            skLineSegment(sketch, "E12.19.6", {"start": v(20.46, -14.95) * mm, "end": v(19.76, -14.38) * mm});
            skArc(sketch, "E12.19.7", {"start": v(18.98, -17) * mm, "mid": v(19.73, -17.22) * mm, "end": v(20.5, -17.35) * mm});
            skPoint(sketch, "E12.19.8", {"position": v(19.2, -13.92) * mm});
            skPoint(sketch, "E12.19.9", {"position": v(18.9, -16.96) * mm});
            skPoint(sketch, "E12.19.10", {"position": v(20.53, -15) * mm});
            skPoint(sketch, "E12.19.11", {"position": v(21.3, -16.7) * mm});
            skArc(sketch, "E12.19.12", {"start": v(21.15, -16.91) * mm, "mid": v(21.24, -16.7) * mm, "end": v(21.22, -16.45) * mm});
            skArc(sketch, "E12.19.13", {"start": v(20.5, -17.35) * mm, "mid": v(20.74, -17.32) * mm, "end": v(20.94, -17.18) * mm});
            skArc(sketch, "E12.19.14", {"start": v(18.84, -16.91) * mm, "mid": v(18.9, -16.96) * mm, "end": v(18.98, -17) * mm});
            skArc(sketch, "E12.19.15", {"start": v(20.57, -15.08) * mm, "mid": v(20.52, -15) * mm, "end": v(20.46, -14.95) * mm});
            skLineSegment(sketch, "E12.19.16", {"start": v(20.94, -17.18) * mm, "end": v(21.33, -16.75) * mm});
            skLineSegment(sketch, "E12.19.17", {"start": v(21.15, -16.91) * mm, "end": v(20.75, -17.46) * mm});
            skPoint(sketch, "E12.20.0", {"position": v(23.93, -12.67) * mm});
            skLineSegment(sketch, "E12.20.1", {"start": v(21.94, -12.62) * mm, "end": v(21.16, -12.23) * mm});
            skArc(sketch, "E12.20.2", {"start": v(21.16, -12.23) * mm, "mid": v(20.8, -12.19) * mm, "end": v(20.5, -12.4) * mm});
            skPoint(sketch, "E12.20.3", {"position": v(20.5, -11.9) * mm});
            skArc(sketch, "E12.20.4", {"start": v(23.26, -10.47) * mm, "mid": v(23.75, -11.05) * mm, "end": v(24.18, -11.68) * mm});
            skArc(sketch, "E12.20.5", {"start": v(22.08, -9.31) * mm, "mid": v(22.07, -9.68) * mm, "end": v(22.32, -9.96) * mm});
            skLineSegment(sketch, "E12.20.6", {"start": v(23.12, -10.37) * mm, "end": v(22.32, -9.96) * mm});
            skArc(sketch, "E12.20.7", {"start": v(22.1, -12.68) * mm, "mid": v(22.88, -12.74) * mm, "end": v(23.66, -12.7) * mm});
            skPoint(sketch, "E12.20.8", {"position": v(21.67, -9.62) * mm});
            skPoint(sketch, "E12.20.9", {"position": v(22.02, -12.66) * mm});
            skPoint(sketch, "E12.20.10", {"position": v(23.2, -10.4) * mm});
            skPoint(sketch, "E12.20.11", {"position": v(24.3, -11.91) * mm});
            skArc(sketch, "E12.20.12", {"start": v(24.2, -12.14) * mm, "mid": v(24.24, -11.91) * mm, "end": v(24.18, -11.68) * mm});
            skArc(sketch, "E12.20.13", {"start": v(23.66, -12.7) * mm, "mid": v(23.89, -12.63) * mm, "end": v(24.05, -12.45) * mm});
            skArc(sketch, "E12.20.14", {"start": v(21.94, -12.62) * mm, "mid": v(22.02, -12.66) * mm, "end": v(22.1, -12.68) * mm});
            skArc(sketch, "E12.20.15", {"start": v(23.26, -10.47) * mm, "mid": v(23.2, -10.41) * mm, "end": v(23.12, -10.37) * mm});
            skLineSegment(sketch, "E12.20.16", {"start": v(24.05, -12.45) * mm, "end": v(24.34, -11.95) * mm});
            skLineSegment(sketch, "E12.20.17", {"start": v(24.2, -12.14) * mm, "end": v(23.93, -12.77) * mm});
            skPoint(sketch, "E12.21.0", {"position": v(26.04, -7.42) * mm});
            skLineSegment(sketch, "E12.21.1", {"start": v(24.09, -7.79) * mm, "end": v(23.24, -7.56) * mm});
            skArc(sketch, "E12.21.2", {"start": v(23.24, -7.56) * mm, "mid": v(22.87, -7.6) * mm, "end": v(22.63, -7.88) * mm});
            skPoint(sketch, "E12.21.3", {"position": v(22.53, -7.37) * mm});
            skArc(sketch, "E12.21.4", {"start": v(24.93, -5.4) * mm, "mid": v(25.53, -5.87) * mm, "end": v(26.08, -6.4) * mm});
            skArc(sketch, "E12.21.5", {"start": v(23.53, -4.52) * mm, "mid": v(23.6, -4.88) * mm, "end": v(23.9, -5.1) * mm});
            skLineSegment(sketch, "E12.21.6", {"start": v(24.77, -5.33) * mm, "end": v(23.9, -5.1) * mm});
            skArc(sketch, "E12.21.7", {"start": v(24.25, -7.8) * mm, "mid": v(25.03, -7.7) * mm, "end": v(25.79, -7.5) * mm});
            skPoint(sketch, "E12.21.8", {"position": v(23.2, -4.9) * mm});
            skPoint(sketch, "E12.21.9", {"position": v(24.17, -7.8) * mm});
            skPoint(sketch, "E12.21.10", {"position": v(24.86, -5.36) * mm});
            skPoint(sketch, "E12.21.11", {"position": v(26.25, -6.6) * mm});
            skArc(sketch, "E12.21.12", {"start": v(26.2, -6.85) * mm, "mid": v(26.2, -6.6) * mm, "end": v(26.08, -6.4) * mm});
            skArc(sketch, "E12.21.13", {"start": v(25.79, -7.5) * mm, "mid": v(26, -7.38) * mm, "end": v(26.11, -7.18) * mm});
            skArc(sketch, "E12.21.14", {"start": v(24.09, -7.79) * mm, "mid": v(24.17, -7.8) * mm, "end": v(24.25, -7.8) * mm});
            skArc(sketch, "E12.21.15", {"start": v(24.93, -5.4) * mm, "mid": v(24.85, -5.36) * mm, "end": v(24.77, -5.33) * mm});
            skLineSegment(sketch, "E12.21.16", {"start": v(26.11, -7.18) * mm, "end": v(26.3, -6.63) * mm});
            skLineSegment(sketch, "E12.21.17", {"start": v(26.2, -6.85) * mm, "end": v(26.06, -7.51) * mm});
            skPoint(sketch, "E12.22.0", {"position": v(27.01, -1.85) * mm});
            skLineSegment(sketch, "E12.22.1", {"start": v(25.18, -2.6) * mm, "end": v(24.3, -2.56) * mm});
            skArc(sketch, "E12.22.2", {"start": v(24.3, -2.56) * mm, "mid": v(23.95, -2.68) * mm, "end": v(23.77, -3) * mm});
            skPoint(sketch, "E12.22.3", {"position": v(23.57, -2.52) * mm});
            skArc(sketch, "E12.22.4", {"start": v(25.5, -0.1) * mm, "mid": v(26.2, -0.43) * mm, "end": v(26.84, -0.84) * mm});
            skArc(sketch, "E12.22.5", {"start": v(23.96, 0.47) * mm, "mid": v(24.1, 0.13) * mm, "end": v(24.44, -0.02) * mm});
            skLineSegment(sketch, "E12.22.6", {"start": v(25.34, -0.07) * mm, "end": v(24.44, -0.02) * mm});
            skArc(sketch, "E12.22.7", {"start": v(25.35, -2.6) * mm, "mid": v(26.08, -2.33) * mm, "end": v(26.79, -1.98) * mm});
            skPoint(sketch, "E12.22.8", {"position": v(23.7, 0.02) * mm});
            skPoint(sketch, "E12.22.9", {"position": v(25.26, -2.61) * mm});
            skPoint(sketch, "E12.22.10", {"position": v(25.43, -0.07) * mm});
            skPoint(sketch, "E12.22.11", {"position": v(27.05, -1) * mm});
            skArc(sketch, "E12.22.12", {"start": v(27.05, -1.25) * mm, "mid": v(27, -1.02) * mm, "end": v(26.84, -0.84) * mm});
            skArc(sketch, "E12.22.13", {"start": v(26.79, -1.98) * mm, "mid": v(26.96, -1.82) * mm, "end": v(27.04, -1.6) * mm});
            skArc(sketch, "E12.22.14", {"start": v(25.18, -2.6) * mm, "mid": v(25.26, -2.6) * mm, "end": v(25.35, -2.6) * mm});
            skArc(sketch, "E12.22.15", {"start": v(25.5, -0.1) * mm, "mid": v(25.43, -0.08) * mm, "end": v(25.34, -0.07) * mm});
            skLineSegment(sketch, "E12.22.16", {"start": v(27.04, -1.6) * mm, "end": v(27.1, -1.02) * mm});
            skLineSegment(sketch, "E12.22.17", {"start": v(27.05, -1.25) * mm, "end": v(27.05, -1.93) * mm});
            skPoint(sketch, "E12.23.0", {"position": v(26.8, 3.81) * mm});
            skLineSegment(sketch, "E12.23.1", {"start": v(25.17, 2.68) * mm, "end": v(24.3, 2.55) * mm});
            skArc(sketch, "E12.23.2", {"start": v(24.3, 2.55) * mm, "mid": v(23.99, 2.36) * mm, "end": v(23.88, 2) * mm});
            skPoint(sketch, "E12.23.3", {"position": v(23.58, 2.43) * mm});
            skArc(sketch, "E12.23.4", {"start": v(24.97, 5.2) * mm, "mid": v(25.71, 5.03) * mm, "end": v(26.43, 4.76) * mm});
            skArc(sketch, "E12.23.5", {"start": v(23.34, 5.44) * mm, "mid": v(23.55, 5.14) * mm, "end": v(23.9, 5.06) * mm});
            skLineSegment(sketch, "E12.23.6", {"start": v(24.8, 5.2) * mm, "end": v(23.9, 5.06) * mm});
            skArc(sketch, "E12.23.7", {"start": v(25.33, 2.74) * mm, "mid": v(26, 3.14) * mm, "end": v(26.61, 3.63) * mm});
            skPoint(sketch, "E12.23.8", {"position": v(23.18, 4.95) * mm});
            skPoint(sketch, "E12.23.9", {"position": v(25.25, 2.7) * mm});
            skPoint(sketch, "E12.23.10", {"position": v(24.88, 5.22) * mm});
            skPoint(sketch, "E12.23.11", {"position": v(26.67, 4.65) * mm});
            skArc(sketch, "E12.23.12", {"start": v(26.72, 4.4) * mm, "mid": v(26.62, 4.61) * mm, "end": v(26.43, 4.76) * mm});
            skArc(sketch, "E12.23.13", {"start": v(26.61, 3.63) * mm, "mid": v(26.75, 3.83) * mm, "end": v(26.78, 4.06) * mm});
            skArc(sketch, "E12.23.14", {"start": v(25.17, 2.68) * mm, "mid": v(25.25, 2.7) * mm, "end": v(25.33, 2.74) * mm});
            skArc(sketch, "E12.23.15", {"start": v(24.97, 5.2) * mm, "mid": v(24.89, 5.21) * mm, "end": v(24.8, 5.2) * mm});
            skLineSegment(sketch, "E12.23.16", {"start": v(26.78, 4.06) * mm, "end": v(26.72, 4.64) * mm});
            skLineSegment(sketch, "E12.23.17", {"start": v(26.72, 4.4) * mm, "end": v(26.86, 3.74) * mm});
            skPoint(sketch, "E12.24.0", {"position": v(25.43, 9.3) * mm});
            skLineSegment(sketch, "E12.24.1", {"start": v(24.06, 7.86) * mm, "end": v(23.24, 7.54) * mm});
            skArc(sketch, "E12.24.2", {"start": v(23.24, 7.54) * mm, "mid": v(22.97, 7.3) * mm, "end": v(22.94, 6.93) * mm});
            skPoint(sketch, "E12.24.3", {"position": v(22.56, 7.28) * mm});
            skArc(sketch, "E12.24.4", {"start": v(23.34, 10.28) * mm, "mid": v(24.1, 10.26) * mm, "end": v(24.86, 10.15) * mm});
            skArc(sketch, "E12.24.5", {"start": v(21.7, 10.17) * mm, "mid": v(21.97, 9.92) * mm, "end": v(22.33, 9.92) * mm});
            skLineSegment(sketch, "E12.24.6", {"start": v(23.18, 10.25) * mm, "end": v(22.33, 9.92) * mm});
            skArc(sketch, "E12.24.7", {"start": v(24.2, 7.94) * mm, "mid": v(24.78, 8.48) * mm, "end": v(25.28, 9.08) * mm});
            skPoint(sketch, "E12.24.8", {"position": v(21.65, 9.66) * mm});
            skPoint(sketch, "E12.24.9", {"position": v(24.14, 7.89) * mm});
            skPoint(sketch, "E12.24.10", {"position": v(23.26, 10.28) * mm});
            skPoint(sketch, "E12.24.11", {"position": v(25.12, 10.1) * mm});
            skArc(sketch, "E12.24.12", {"start": v(25.22, 9.86) * mm, "mid": v(25.07, 10.05) * mm, "end": v(24.86, 10.15) * mm});
            skArc(sketch, "E12.24.13", {"start": v(25.28, 9.08) * mm, "mid": v(25.37, 9.3) * mm, "end": v(25.35, 9.54) * mm});
            skArc(sketch, "E12.24.14", {"start": v(24.06, 7.86) * mm, "mid": v(24.14, 7.9) * mm, "end": v(24.2, 7.94) * mm});
            skArc(sketch, "E12.24.15", {"start": v(23.34, 10.28) * mm, "mid": v(23.26, 10.27) * mm, "end": v(23.18, 10.25) * mm});
            skLineSegment(sketch, "E12.24.16", {"start": v(25.35, 9.54) * mm, "end": v(25.17, 10.1) * mm});
            skLineSegment(sketch, "E12.24.17", {"start": v(25.22, 9.86) * mm, "end": v(25.5, 9.24) * mm});
            skPoint(sketch, "E12.25.0", {"position": v(22.94, 14.38) * mm});
            skLineSegment(sketch, "E12.25.1", {"start": v(21.9, 12.7) * mm, "end": v(21.17, 12.21) * mm});
            skArc(sketch, "E12.25.2", {"start": v(21.17, 12.21) * mm, "mid": v(20.95, 11.91) * mm, "end": v(21, 11.55) * mm});
            skPoint(sketch, "E12.25.3", {"position": v(20.55, 11.81) * mm});
            skArc(sketch, "E12.25.4", {"start": v(20.7, 14.9) * mm, "mid": v(21.45, 15.05) * mm, "end": v(22.2, 15.1) * mm});
            skArc(sketch, "E12.25.5", {"start": v(19.1, 14.46) * mm, "mid": v(19.42, 14.27) * mm, "end": v(19.78, 14.35) * mm});
            skLineSegment(sketch, "E12.25.6", {"start": v(20.54, 14.84) * mm, "end": v(19.78, 14.35) * mm});
            skArc(sketch, "E12.25.7", {"start": v(22.03, 12.8) * mm, "mid": v(22.47, 13.45) * mm, "end": v(22.83, 14.14) * mm});
            skPoint(sketch, "E12.25.8", {"position": v(19.17, 13.95) * mm});
            skPoint(sketch, "E12.25.9", {"position": v(21.97, 12.74) * mm});
            skPoint(sketch, "E12.25.10", {"position": v(20.61, 14.89) * mm});
            skPoint(sketch, "E12.25.11", {"position": v(22.47, 15.1) * mm});
            skArc(sketch, "E12.25.12", {"start": v(22.62, 14.89) * mm, "mid": v(22.44, 15.04) * mm, "end": v(22.2, 15.1) * mm});
            skArc(sketch, "E12.25.13", {"start": v(22.83, 14.14) * mm, "mid": v(22.88, 14.37) * mm, "end": v(22.81, 14.6) * mm});
            skArc(sketch, "E12.25.14", {"start": v(21.9, 12.7) * mm, "mid": v(21.97, 12.74) * mm, "end": v(22.03, 12.8) * mm});
            skArc(sketch, "E12.25.15", {"start": v(20.7, 14.9) * mm, "mid": v(20.62, 14.88) * mm, "end": v(20.54, 14.84) * mm});
            skLineSegment(sketch, "E12.25.16", {"start": v(22.81, 14.6) * mm, "end": v(22.52, 15.1) * mm});
            skLineSegment(sketch, "E12.25.17", {"start": v(22.62, 14.89) * mm, "end": v(23.02, 14.34) * mm});
            skPoint(sketch, "E12.26.0", {"position": v(19.44, 18.84) * mm});
            skLineSegment(sketch, "E12.26.1", {"start": v(18.79, 16.97) * mm, "end": v(18.17, 16.34) * mm});
            skArc(sketch, "E12.26.2", {"start": v(18.17, 16.34) * mm, "mid": v(18.02, 16) * mm, "end": v(18.14, 15.66) * mm});
            skPoint(sketch, "E12.26.3", {"position": v(17.65, 15.83) * mm});
            skArc(sketch, "E12.26.4", {"start": v(17.14, 18.89) * mm, "mid": v(17.85, 19.18) * mm, "end": v(18.58, 19.38) * mm});
            skArc(sketch, "E12.26.5", {"start": v(15.68, 18.12) * mm, "mid": v(16.03, 18) * mm, "end": v(16.37, 18.15) * mm});
            skLineSegment(sketch, "E12.26.6", {"start": v(17, 18.79) * mm, "end": v(16.37, 18.15) * mm});
            skArc(sketch, "E12.26.7", {"start": v(18.88, 17.1) * mm, "mid": v(19.19, 17.83) * mm, "end": v(19.4, 18.58) * mm});
            skPoint(sketch, "E12.26.8", {"position": v(15.85, 17.63) * mm});
            skPoint(sketch, "E12.26.9", {"position": v(18.85, 17.03) * mm});
            skPoint(sketch, "E12.26.10", {"position": v(17.07, 18.85) * mm});
            skPoint(sketch, "E12.26.11", {"position": v(18.84, 19.43) * mm});
            skArc(sketch, "E12.26.12", {"start": v(19.03, 19.26) * mm, "mid": v(18.82, 19.38) * mm, "end": v(18.58, 19.38) * mm});
            skArc(sketch, "E12.26.13", {"start": v(19.4, 18.58) * mm, "mid": v(19.39, 18.82) * mm, "end": v(19.28, 19.03) * mm});
            skArc(sketch, "E12.26.14", {"start": v(18.79, 16.97) * mm, "mid": v(18.84, 17.03) * mm, "end": v(18.88, 17.1) * mm});
            skArc(sketch, "E12.26.15", {"start": v(17.14, 18.89) * mm, "mid": v(17.07, 18.84) * mm, "end": v(17, 18.79) * mm});
            skLineSegment(sketch, "E12.26.16", {"start": v(19.28, 19.03) * mm, "end": v(18.89, 19.46) * mm});
            skLineSegment(sketch, "E12.26.17", {"start": v(19.03, 19.26) * mm, "end": v(19.53, 18.8) * mm});
            skPoint(sketch, "E12.27.0", {"position": v(15.1, 22.47) * mm});
            skLineSegment(sketch, "E12.27.1", {"start": v(14.85, 20.5) * mm, "end": v(14.37, 19.76) * mm});
            skArc(sketch, "E12.27.2", {"start": v(14.37, 19.76) * mm, "mid": v(14.3, 19.4) * mm, "end": v(14.48, 19.09) * mm});
            skPoint(sketch, "E12.27.3", {"position": v(13.97, 19.15) * mm});
            skArc(sketch, "E12.27.4", {"start": v(12.84, 22.04) * mm, "mid": v(13.47, 22.47) * mm, "end": v(14.15, 22.82) * mm});
            skArc(sketch, "E12.27.5", {"start": v(11.57, 20.98) * mm, "mid": v(11.94, 20.94) * mm, "end": v(12.24, 21.16) * mm});
            skLineSegment(sketch, "E12.27.6", {"start": v(12.73, 21.91) * mm, "end": v(12.24, 21.16) * mm});
            skArc(sketch, "E12.27.7", {"start": v(14.92, 20.65) * mm, "mid": v(15.06, 21.42) * mm, "end": v(15.1, 22.2) * mm});
            skPoint(sketch, "E12.27.8", {"position": v(11.84, 20.54) * mm});
            skPoint(sketch, "E12.27.9", {"position": v(14.9, 20.57) * mm});
            skPoint(sketch, "E12.27.10", {"position": v(12.77, 21.98) * mm});
            skPoint(sketch, "E12.27.11", {"position": v(14.39, 22.93) * mm});
            skArc(sketch, "E12.27.12", {"start": v(14.6, 22.8) * mm, "mid": v(14.38, 22.87) * mm, "end": v(14.15, 22.82) * mm});
            skArc(sketch, "E12.27.13", {"start": v(15.1, 22.2) * mm, "mid": v(15.05, 22.44) * mm, "end": v(14.9, 22.62) * mm});
            skArc(sketch, "E12.27.14", {"start": v(14.85, 20.5) * mm, "mid": v(14.89, 20.58) * mm, "end": v(14.92, 20.65) * mm});
            skArc(sketch, "E12.27.15", {"start": v(12.84, 22.04) * mm, "mid": v(12.78, 21.98) * mm, "end": v(12.73, 21.91) * mm});
            skLineSegment(sketch, "E12.27.16", {"start": v(14.9, 22.62) * mm, "end": v(14.43, 22.96) * mm});
            skLineSegment(sketch, "E12.27.17", {"start": v(14.6, 22.8) * mm, "end": v(15.2, 22.46) * mm});
            skPoint(sketch, "E12.28.0", {"position": v(10.1, 25.12) * mm});
            skLineSegment(sketch, "E12.28.1", {"start": v(10.26, 23.14) * mm, "end": v(9.95, 22.32) * mm});
            skArc(sketch, "E12.28.2", {"start": v(9.95, 22.32) * mm, "mid": v(9.95, 21.95) * mm, "end": v(10.2, 21.68) * mm});
            skPoint(sketch, "E12.28.3", {"position": v(9.68, 21.64) * mm});
            skArc(sketch, "E12.28.4", {"start": v(7.98, 24.23) * mm, "mid": v(8.5, 24.78) * mm, "end": v(9.1, 25.27) * mm});
            skArc(sketch, "E12.28.5", {"start": v(6.96, 22.93) * mm, "mid": v(7.32, 22.96) * mm, "end": v(7.57, 23.24) * mm});
            skLineSegment(sketch, "E12.28.6", {"start": v(7.9, 24.08) * mm, "end": v(7.57, 23.24) * mm});
            skArc(sketch, "E12.28.7", {"start": v(10.3, 23.3) * mm, "mid": v(10.28, 24.09) * mm, "end": v(10.16, 24.86) * mm});
            skPoint(sketch, "E12.28.8", {"position": v(7.3, 22.55) * mm});
            skPoint(sketch, "E12.28.9", {"position": v(10.3, 23.22) * mm});
            skPoint(sketch, "E12.28.10", {"position": v(7.92, 24.16) * mm});
            skPoint(sketch, "E12.28.11", {"position": v(9.3, 25.42) * mm});
            skArc(sketch, "E12.28.12", {"start": v(9.55, 25.34) * mm, "mid": v(9.31, 25.36) * mm, "end": v(9.1, 25.27) * mm});
            skArc(sketch, "E12.28.13", {"start": v(10.16, 24.86) * mm, "mid": v(10.06, 25.08) * mm, "end": v(9.87, 25.22) * mm});
            skArc(sketch, "E12.28.14", {"start": v(10.26, 23.14) * mm, "mid": v(10.29, 23.22) * mm, "end": v(10.3, 23.3) * mm});
            skArc(sketch, "E12.28.15", {"start": v(7.98, 24.23) * mm, "mid": v(7.93, 24.16) * mm, "end": v(7.9, 24.08) * mm});
            skLineSegment(sketch, "E12.28.16", {"start": v(9.87, 25.22) * mm, "end": v(9.34, 25.46) * mm});
            skLineSegment(sketch, "E12.28.17", {"start": v(9.55, 25.34) * mm, "end": v(10.2, 25.13) * mm});
            skPoint(sketch, "E12.29.0", {"position": v(4.66, 26.67) * mm});
            skLineSegment(sketch, "E12.29.1", {"start": v(5.23, 24.77) * mm, "end": v(5.09, 23.9) * mm});
            skArc(sketch, "E12.29.2", {"start": v(5.09, 23.9) * mm, "mid": v(5.17, 23.54) * mm, "end": v(5.47, 23.33) * mm});
            skPoint(sketch, "E12.29.3", {"position": v(4.97, 23.18) * mm});
            skArc(sketch, "E12.29.4", {"start": v(2.77, 25.36) * mm, "mid": v(3.17, 26) * mm, "end": v(3.64, 26.6) * mm});
            skArc(sketch, "E12.29.5", {"start": v(2.04, 23.88) * mm, "mid": v(2.39, 23.98) * mm, "end": v(2.57, 24.3) * mm});
            skLineSegment(sketch, "E12.29.6", {"start": v(2.71, 25.2) * mm, "end": v(2.57, 24.3) * mm});
            skArc(sketch, "E12.29.7", {"start": v(5.23, 24.94) * mm, "mid": v(5.04, 25.7) * mm, "end": v(4.77, 26.43) * mm});
            skPoint(sketch, "E12.29.8", {"position": v(2.46, 23.58) * mm});
            skPoint(sketch, "E12.29.9", {"position": v(5.24, 24.85) * mm});
            skPoint(sketch, "E12.29.10", {"position": v(2.73, 25.28) * mm});
            skPoint(sketch, "E12.29.11", {"position": v(3.82, 26.8) * mm});
            skArc(sketch, "E12.29.12", {"start": v(4.07, 26.77) * mm, "mid": v(3.84, 26.74) * mm, "end": v(3.64, 26.6) * mm});
            skArc(sketch, "E12.29.13", {"start": v(4.77, 26.43) * mm, "mid": v(4.63, 26.62) * mm, "end": v(4.41, 26.72) * mm});
            skArc(sketch, "E12.29.14", {"start": v(5.23, 24.77) * mm, "mid": v(5.23, 24.85) * mm, "end": v(5.23, 24.94) * mm});
            skArc(sketch, "E12.29.15", {"start": v(2.77, 25.36) * mm, "mid": v(2.73, 25.28) * mm, "end": v(2.71, 25.2) * mm});
            skLineSegment(sketch, "E12.29.16", {"start": v(4.41, 26.72) * mm, "end": v(3.84, 26.84) * mm});
            skLineSegment(sketch, "E12.29.17", {"start": v(4.07, 26.77) * mm, "end": v(4.75, 26.7) * mm});
            skPoint(sketch, "E12.center", {"position": v(0, 0) * mm});
            skLineSegment(sketch, "E13", {"start": v(0.5, 23.96) * mm, "end": v(2.04, 23.88) * mm});
            skLineSegment(sketch, "E14.1.0", {"start": v(-4.5, 23.54) * mm, "end": v(-2.97, 23.78) * mm});
            skLineSegment(sketch, "E14.2.0", {"start": v(-9.29, 22.09) * mm, "end": v(-7.85, 22.64) * mm});
            skLineSegment(sketch, "E14.3.0", {"start": v(-13.68, 19.67) * mm, "end": v(-12.39, 20.51) * mm});
            skLineSegment(sketch, "E14.4.0", {"start": v(-17.47, 16.4) * mm, "end": v(-16.38, 17.49) * mm});
            skLineSegment(sketch, "E14.5.0", {"start": v(-20.5, 12.4) * mm, "end": v(-19.66, 13.7) * mm});
            skLineSegment(sketch, "E14.6.0", {"start": v(-22.63, 7.88) * mm, "end": v(-22.08, 9.31) * mm});
            skLineSegment(sketch, "E14.7.0", {"start": v(-23.77, 3) * mm, "end": v(-23.53, 4.52) * mm});
            skLineSegment(sketch, "E14.8.0", {"start": v(-23.88, -2) * mm, "end": v(-23.96, -0.47) * mm});
            skLineSegment(sketch, "E14.9.0", {"start": v(-22.94, -6.93) * mm, "end": v(-23.34, -5.44) * mm});
            skLineSegment(sketch, "E14.10.0", {"start": v(-21, -11.55) * mm, "end": v(-21.7, -10.17) * mm});
            skLineSegment(sketch, "E14.11.0", {"start": v(-18.14, -15.66) * mm, "end": v(-19.1, -14.46) * mm});
            skLineSegment(sketch, "E14.12.0", {"start": v(-14.48, -19.09) * mm, "end": v(-15.68, -18.12) * mm});
            skLineSegment(sketch, "E14.13.0", {"start": v(-10.2, -21.68) * mm, "end": v(-11.57, -20.98) * mm});
            skLineSegment(sketch, "E14.14.0", {"start": v(-5.47, -23.33) * mm, "end": v(-6.96, -22.93) * mm});
            skLineSegment(sketch, "E14.15.0", {"start": v(-0.5, -23.96) * mm, "end": v(-2.04, -23.88) * mm});
            skLineSegment(sketch, "E14.16.0", {"start": v(4.5, -23.54) * mm, "end": v(2.97, -23.78) * mm});
            skLineSegment(sketch, "E14.17.0", {"start": v(9.29, -22.09) * mm, "end": v(7.85, -22.64) * mm});
            skLineSegment(sketch, "E14.18.0", {"start": v(13.68, -19.67) * mm, "end": v(12.39, -20.51) * mm});
            skLineSegment(sketch, "E14.19.0", {"start": v(17.47, -16.4) * mm, "end": v(16.38, -17.49) * mm});
            skLineSegment(sketch, "E14.20.0", {"start": v(20.5, -12.4) * mm, "end": v(19.66, -13.7) * mm});
            skLineSegment(sketch, "E14.21.0", {"start": v(22.63, -7.88) * mm, "end": v(22.08, -9.31) * mm});
            skLineSegment(sketch, "E14.22.0", {"start": v(23.77, -3) * mm, "end": v(23.53, -4.52) * mm});
            skLineSegment(sketch, "E14.23.0", {"start": v(23.88, 2) * mm, "end": v(23.96, 0.47) * mm});
            skLineSegment(sketch, "E14.24.0", {"start": v(22.94, 6.93) * mm, "end": v(23.34, 5.44) * mm});
            skLineSegment(sketch, "E14.25.0", {"start": v(21, 11.55) * mm, "end": v(21.7, 10.17) * mm});
            skLineSegment(sketch, "E14.26.0", {"start": v(18.14, 15.66) * mm, "end": v(19.1, 14.46) * mm});
            skLineSegment(sketch, "E14.27.0", {"start": v(14.48, 19.09) * mm, "end": v(15.68, 18.12) * mm});
            skLineSegment(sketch, "E14.28.0", {"start": v(10.2, 21.68) * mm, "end": v(11.57, 20.98) * mm});
            skLineSegment(sketch, "E14.29.0", {"start": v(5.47, 23.33) * mm, "end": v(6.96, 22.93) * mm});
            skSolve(sketch);
        }
        {
            var Q0;
            Q0=qCreatedBy(makeId("Front.planeOp"),FACE);
            cPlane(context, id + "F1", {"entities" : qUnion([Q0]), "cplaneType" : CPlaneType.OFFSET, "offset" : 22 * mm, "oppositeDirection" : true, "width" : 152.4 * mm, "height" : 152.4 * mm});
        }
        {
            var Q0;
            Q0=qCreatedBy(id+"F1.planeOp",FACE);
            var sketch = newSketch(context, id + "F2", { "sketchPlane" : qUnion([Q0])});
            skArc(sketch, "E15", {"start": v(-0.1, 38.37) * mm, "mid": v(-0.63, 39.42) * mm, "end": v(-1.27, 40.4) * mm});
            skLineSegment(sketch, "E16", {"start": v(-1.7, 40.6) * mm, "end": v(-2.13, 40.58) * mm});
            skLineSegment(sketch, "E17", {"start": v(0.01, 37.84) * mm, "end": v(0.1, 36.04) * mm});
            skLineSegment(sketch, "E18.MirrorCS", {"start": v(-2.55, 40.56) * mm, "end": v(-2.13, 40.58) * mm});
            skArc(sketch, "E19.MirrorCS", {"start": v(-3.9, 38.17) * mm, "mid": v(-3.5, 39.27) * mm, "end": v(-2.96, 40.3) * mm});
            skLineSegment(sketch, "E20.MirrorCS", {"start": v(-3.97, 37.63) * mm, "end": v(-3.87, 35.83) * mm});
            skPoint(sketch, "E21.visualSharp", {"position": v(0, 38.1) * mm});
            skArc(sketch, "E21.filletArc", {"start": v(0.01, 37.84) * mm, "mid": v(-0.02, 38.1) * mm, "end": v(-0.1, 38.37) * mm});
            skPoint(sketch, "E22.visualSharp", {"position": v(-3.98, 37.9) * mm});
            skArc(sketch, "E22.filletArc", {"start": v(-3.9, 38.17) * mm, "mid": v(-3.96, 37.9) * mm, "end": v(-3.97, 37.63) * mm});
            skPoint(sketch, "E23.visualSharp", {"position": v(-1.44, 40.61) * mm});
            skArc(sketch, "E23.filletArc", {"start": v(-1.27, 40.4) * mm, "mid": v(-1.46, 40.55) * mm, "end": v(-1.7, 40.6) * mm});
            skPoint(sketch, "E24.visualSharp", {"position": v(-2.81, 40.54) * mm});
            skArc(sketch, "E24.filletArc", {"start": v(-2.55, 40.56) * mm, "mid": v(-2.78, 40.48) * mm, "end": v(-2.96, 40.3) * mm});
            skPoint(sketch, "E25.visualSharp", {"position": v(-3.85, 35.35) * mm});
            skArc(sketch, "E25.filletArc", {"start": v(-4.32, 35.3) * mm, "mid": v(-4, 35.47) * mm, "end": v(-3.87, 35.83) * mm});
            skPoint(sketch, "E26.visualSharp", {"position": v(0.13, 35.56) * mm});
            skArc(sketch, "E26.filletArc", {"start": v(0.1, 36.04) * mm, "mid": v(0.26, 35.7) * mm, "end": v(0.6, 35.55) * mm});
            skPoint(sketch, "E27.1.0", {"position": v(-11.18, 39.07) * mm});
            skPoint(sketch, "E27.1.1", {"position": v(-11.77, 36.24) * mm});
            skArc(sketch, "E27.1.2", {"start": v(-11.75, 36.52) * mm, "mid": v(-11.58, 37.68) * mm, "end": v(-11.27, 38.81) * mm});
            skPoint(sketch, "E27.1.3", {"position": v(-11.12, 33.78) * mm});
            skPoint(sketch, "E27.1.4", {"position": v(-7.26, 34.81) * mm});
            skLineSegment(sketch, "E27.1.5", {"start": v(-11.7, 35.98) * mm, "end": v(-11.24, 34.24) * mm});
            skPoint(sketch, "E27.1.6", {"position": v(-9.85, 39.43) * mm});
            skLineSegment(sketch, "E27.1.7", {"start": v(-7.85, 37.01) * mm, "end": v(-7.39, 35.27) * mm});
            skArc(sketch, "E27.1.8", {"start": v(-8.08, 37.5) * mm, "mid": v(-8.8, 38.43) * mm, "end": v(-9.64, 39.25) * mm});
            skPoint(sketch, "E27.1.9", {"position": v(-7.92, 37.27) * mm});
            skArc(sketch, "E27.1.10", {"start": v(-11.56, 33.63) * mm, "mid": v(-11.28, 33.87) * mm, "end": v(-11.24, 34.24) * mm});
            skArc(sketch, "E27.1.11", {"start": v(-7.39, 35.27) * mm, "mid": v(-7.16, 34.97) * mm, "end": v(-6.8, 34.9) * mm});
            skArc(sketch, "E27.1.12", {"start": v(-7.85, 37.01) * mm, "mid": v(-7.95, 37.27) * mm, "end": v(-8.08, 37.5) * mm});
            skArc(sketch, "E27.1.13", {"start": v(-10.92, 39.14) * mm, "mid": v(-11.14, 39.02) * mm, "end": v(-11.27, 38.81) * mm});
            skArc(sketch, "E27.1.14", {"start": v(-9.64, 39.25) * mm, "mid": v(-9.86, 39.36) * mm, "end": v(-10.1, 39.36) * mm});
            skArc(sketch, "E27.1.15", {"start": v(-11.75, 36.52) * mm, "mid": v(-11.75, 36.25) * mm, "end": v(-11.7, 35.98) * mm});
            skLineSegment(sketch, "E27.1.16", {"start": v(-10.92, 39.14) * mm, "end": v(-10.52, 39.25) * mm});
            skLineSegment(sketch, "E27.1.17", {"start": v(-10.1, 39.36) * mm, "end": v(-10.52, 39.25) * mm});
            skPoint(sketch, "E27.2.0", {"position": v(-19.06, 35.9) * mm});
            skPoint(sketch, "E27.2.1", {"position": v(-19.05, 33) * mm});
            skArc(sketch, "E27.2.2", {"start": v(-19.1, 33.28) * mm, "mid": v(-19.17, 34.45) * mm, "end": v(-19.1, 35.62) * mm});
            skPoint(sketch, "E27.2.3", {"position": v(-17.9, 30.73) * mm});
            skPoint(sketch, "E27.2.4", {"position": v(-14.34, 32.54) * mm});
            skLineSegment(sketch, "E27.2.5", {"start": v(-18.93, 32.76) * mm, "end": v(-18.11, 31.15) * mm});
            skPoint(sketch, "E27.2.6", {"position": v(-17.83, 36.52) * mm});
            skLineSegment(sketch, "E27.2.7", {"start": v(-15.38, 34.57) * mm, "end": v(-14.56, 32.96) * mm});
            skArc(sketch, "E27.2.8", {"start": v(-15.7, 35) * mm, "mid": v(-16.6, 35.76) * mm, "end": v(-17.6, 36.39) * mm});
            skPoint(sketch, "E27.2.9", {"position": v(-15.5, 34.8) * mm});
            skArc(sketch, "E27.2.10", {"start": v(-18.3, 30.49) * mm, "mid": v(-18.08, 30.78) * mm, "end": v(-18.11, 31.15) * mm});
            skArc(sketch, "E27.2.11", {"start": v(-14.56, 32.96) * mm, "mid": v(-14.28, 32.72) * mm, "end": v(-13.9, 32.73) * mm});
            skArc(sketch, "E27.2.12", {"start": v(-15.38, 34.57) * mm, "mid": v(-15.52, 34.8) * mm, "end": v(-15.7, 35) * mm});
            skArc(sketch, "E27.2.13", {"start": v(-18.82, 36.01) * mm, "mid": v(-19, 35.85) * mm, "end": v(-19.1, 35.62) * mm});
            skArc(sketch, "E27.2.14", {"start": v(-17.6, 36.39) * mm, "mid": v(-17.83, 36.45) * mm, "end": v(-18.07, 36.4) * mm});
            skArc(sketch, "E27.2.15", {"start": v(-19.1, 33.28) * mm, "mid": v(-19.03, 33.01) * mm, "end": v(-18.93, 32.76) * mm});
            skLineSegment(sketch, "E27.2.16", {"start": v(-18.82, 36.01) * mm, "end": v(-18.45, 36.2) * mm});
            skLineSegment(sketch, "E27.2.17", {"start": v(-18.07, 36.4) * mm, "end": v(-18.45, 36.2) * mm});
            skPoint(sketch, "E27.3.0", {"position": v(-26.1, 31.15) * mm});
            skPoint(sketch, "E27.3.1", {"position": v(-25.5, 28.31) * mm});
            skArc(sketch, "E27.3.2", {"start": v(-25.6, 28.59) * mm, "mid": v(-25.91, 29.71) * mm, "end": v(-26.09, 30.87) * mm});
            skPoint(sketch, "E27.3.3", {"position": v(-23.9, 26.34) * mm});
            skPoint(sketch, "E27.3.4", {"position": v(-20.8, 28.85) * mm});
            skLineSegment(sketch, "E27.3.5", {"start": v(-25.33, 28.1) * mm, "end": v(-24.2, 26.7) * mm});
            skPoint(sketch, "E27.3.6", {"position": v(-25.04, 32.01) * mm});
            skLineSegment(sketch, "E27.3.7", {"start": v(-22.23, 30.62) * mm, "end": v(-21.1, 29.22) * mm});
            skArc(sketch, "E27.3.8", {"start": v(-22.64, 30.98) * mm, "mid": v(-23.68, 31.52) * mm, "end": v(-24.77, 31.94) * mm});
            skPoint(sketch, "E27.3.9", {"position": v(-22.4, 30.82) * mm});
            skArc(sketch, "E27.3.10", {"start": v(-24.24, 26.02) * mm, "mid": v(-24.08, 26.35) * mm, "end": v(-24.2, 26.7) * mm});
            skArc(sketch, "E27.3.11", {"start": v(-21.1, 29.22) * mm, "mid": v(-20.77, 29.03) * mm, "end": v(-20.4, 29.12) * mm});
            skArc(sketch, "E27.3.12", {"start": v(-22.23, 30.62) * mm, "mid": v(-22.42, 30.82) * mm, "end": v(-22.64, 30.98) * mm});
            skArc(sketch, "E27.3.13", {"start": v(-25.9, 31.31) * mm, "mid": v(-26.05, 31.12) * mm, "end": v(-26.09, 30.87) * mm});
            skArc(sketch, "E27.3.14", {"start": v(-24.77, 31.94) * mm, "mid": v(-25.02, 31.95) * mm, "end": v(-25.24, 31.84) * mm});
            skArc(sketch, "E27.3.15", {"start": v(-25.6, 28.59) * mm, "mid": v(-25.48, 28.34) * mm, "end": v(-25.33, 28.1) * mm});
            skLineSegment(sketch, "E27.3.16", {"start": v(-25.9, 31.31) * mm, "end": v(-25.57, 31.58) * mm});
            skLineSegment(sketch, "E27.3.17", {"start": v(-25.24, 31.84) * mm, "end": v(-25.57, 31.58) * mm});
            skPoint(sketch, "E27.4.0", {"position": v(-32.01, 25.04) * mm});
            skPoint(sketch, "E27.4.1", {"position": v(-30.82, 22.4) * mm});
            skArc(sketch, "E27.4.2", {"start": v(-30.98, 22.64) * mm, "mid": v(-31.52, 23.68) * mm, "end": v(-31.94, 24.77) * mm});
            skPoint(sketch, "E27.4.3", {"position": v(-28.85, 20.8) * mm});
            skPoint(sketch, "E27.4.4", {"position": v(-26.34, 23.9) * mm});
            skLineSegment(sketch, "E27.4.5", {"start": v(-30.62, 22.23) * mm, "end": v(-29.22, 21.1) * mm});
            skPoint(sketch, "E27.4.6", {"position": v(-31.15, 26.1) * mm});
            skLineSegment(sketch, "E27.4.7", {"start": v(-28.1, 25.33) * mm, "end": v(-26.7, 24.2) * mm});
            skArc(sketch, "E27.4.8", {"start": v(-28.59, 25.6) * mm, "mid": v(-29.71, 25.91) * mm, "end": v(-30.87, 26.09) * mm});
            skPoint(sketch, "E27.4.9", {"position": v(-28.31, 25.5) * mm});
            skArc(sketch, "E27.4.10", {"start": v(-29.12, 20.4) * mm, "mid": v(-29.03, 20.77) * mm, "end": v(-29.22, 21.1) * mm});
            skArc(sketch, "E27.4.11", {"start": v(-26.7, 24.2) * mm, "mid": v(-26.35, 24.08) * mm, "end": v(-26.02, 24.24) * mm});
            skArc(sketch, "E27.4.12", {"start": v(-28.1, 25.33) * mm, "mid": v(-28.34, 25.48) * mm, "end": v(-28.59, 25.6) * mm});
            skArc(sketch, "E27.4.13", {"start": v(-31.84, 25.24) * mm, "mid": v(-31.95, 25.02) * mm, "end": v(-31.94, 24.77) * mm});
            skArc(sketch, "E27.4.14", {"start": v(-30.87, 26.09) * mm, "mid": v(-31.12, 26.05) * mm, "end": v(-31.31, 25.9) * mm});
            skArc(sketch, "E27.4.15", {"start": v(-30.98, 22.64) * mm, "mid": v(-30.82, 22.42) * mm, "end": v(-30.62, 22.23) * mm});
            skLineSegment(sketch, "E27.4.16", {"start": v(-31.84, 25.24) * mm, "end": v(-31.58, 25.57) * mm});
            skLineSegment(sketch, "E27.4.17", {"start": v(-31.31, 25.9) * mm, "end": v(-31.58, 25.57) * mm});
            skPoint(sketch, "E27.5.0", {"position": v(-36.52, 17.83) * mm});
            skPoint(sketch, "E27.5.1", {"position": v(-34.8, 15.5) * mm});
            skArc(sketch, "E27.5.2", {"start": v(-35, 15.7) * mm, "mid": v(-35.76, 16.6) * mm, "end": v(-36.39, 17.6) * mm});
            skPoint(sketch, "E27.5.3", {"position": v(-32.54, 14.34) * mm});
            skPoint(sketch, "E27.5.4", {"position": v(-30.73, 17.9) * mm});
            skLineSegment(sketch, "E27.5.5", {"start": v(-34.57, 15.38) * mm, "end": v(-32.96, 14.56) * mm});
            skPoint(sketch, "E27.5.6", {"position": v(-35.9, 19.06) * mm});
            skLineSegment(sketch, "E27.5.7", {"start": v(-32.76, 18.93) * mm, "end": v(-31.15, 18.11) * mm});
            skArc(sketch, "E27.5.8", {"start": v(-33.28, 19.1) * mm, "mid": v(-34.45, 19.17) * mm, "end": v(-35.62, 19.1) * mm});
            skPoint(sketch, "E27.5.9", {"position": v(-33, 19.05) * mm});
            skArc(sketch, "E27.5.10", {"start": v(-32.73, 13.9) * mm, "mid": v(-32.72, 14.28) * mm, "end": v(-32.96, 14.56) * mm});
            skArc(sketch, "E27.5.11", {"start": v(-31.15, 18.11) * mm, "mid": v(-30.78, 18.08) * mm, "end": v(-30.49, 18.3) * mm});
            skArc(sketch, "E27.5.12", {"start": v(-32.76, 18.93) * mm, "mid": v(-33.01, 19.03) * mm, "end": v(-33.28, 19.1) * mm});
            skArc(sketch, "E27.5.13", {"start": v(-36.4, 18.07) * mm, "mid": v(-36.45, 17.83) * mm, "end": v(-36.39, 17.6) * mm});
            skArc(sketch, "E27.5.14", {"start": v(-35.62, 19.1) * mm, "mid": v(-35.85, 19) * mm, "end": v(-36.01, 18.82) * mm});
            skArc(sketch, "E27.5.15", {"start": v(-35, 15.7) * mm, "mid": v(-34.8, 15.52) * mm, "end": v(-34.57, 15.38) * mm});
            skLineSegment(sketch, "E27.5.16", {"start": v(-36.4, 18.07) * mm, "end": v(-36.2, 18.45) * mm});
            skLineSegment(sketch, "E27.5.17", {"start": v(-36.01, 18.82) * mm, "end": v(-36.2, 18.45) * mm});
            skPoint(sketch, "E27.6.0", {"position": v(-39.43, 9.85) * mm});
            skPoint(sketch, "E27.6.1", {"position": v(-37.27, 7.92) * mm});
            skArc(sketch, "E27.6.2", {"start": v(-37.5, 8.08) * mm, "mid": v(-38.43, 8.8) * mm, "end": v(-39.25, 9.64) * mm});
            skPoint(sketch, "E27.6.3", {"position": v(-34.81, 7.26) * mm});
            skPoint(sketch, "E27.6.4", {"position": v(-33.78, 11.12) * mm});
            skLineSegment(sketch, "E27.6.5", {"start": v(-37.01, 7.85) * mm, "end": v(-35.27, 7.39) * mm});
            skPoint(sketch, "E27.6.6", {"position": v(-39.07, 11.18) * mm});
            skLineSegment(sketch, "E27.6.7", {"start": v(-35.98, 11.7) * mm, "end": v(-34.24, 11.24) * mm});
            skArc(sketch, "E27.6.8", {"start": v(-36.52, 11.75) * mm, "mid": v(-37.68, 11.58) * mm, "end": v(-38.81, 11.27) * mm});
            skPoint(sketch, "E27.6.9", {"position": v(-36.24, 11.77) * mm});
            skArc(sketch, "E27.6.10", {"start": v(-34.9, 6.8) * mm, "mid": v(-34.97, 7.16) * mm, "end": v(-35.27, 7.39) * mm});
            skArc(sketch, "E27.6.11", {"start": v(-34.24, 11.24) * mm, "mid": v(-33.87, 11.28) * mm, "end": v(-33.63, 11.56) * mm});
            skArc(sketch, "E27.6.12", {"start": v(-35.98, 11.7) * mm, "mid": v(-36.25, 11.75) * mm, "end": v(-36.52, 11.75) * mm});
            skArc(sketch, "E27.6.13", {"start": v(-39.36, 10.1) * mm, "mid": v(-39.36, 9.86) * mm, "end": v(-39.25, 9.64) * mm});
            skArc(sketch, "E27.6.14", {"start": v(-38.81, 11.27) * mm, "mid": v(-39.02, 11.14) * mm, "end": v(-39.14, 10.92) * mm});
            skArc(sketch, "E27.6.15", {"start": v(-37.5, 8.08) * mm, "mid": v(-37.27, 7.95) * mm, "end": v(-37.01, 7.85) * mm});
            skLineSegment(sketch, "E27.6.16", {"start": v(-39.36, 10.1) * mm, "end": v(-39.25, 10.52) * mm});
            skLineSegment(sketch, "E27.6.17", {"start": v(-39.14, 10.92) * mm, "end": v(-39.25, 10.52) * mm});
            skPoint(sketch, "E27.7.0", {"position": v(-40.61, 1.44) * mm});
            skPoint(sketch, "E27.7.1", {"position": v(-38.1, 0) * mm});
            skArc(sketch, "E27.7.2", {"start": v(-38.37, 0.1) * mm, "mid": v(-39.42, 0.63) * mm, "end": v(-40.4, 1.27) * mm});
            skPoint(sketch, "E27.7.3", {"position": v(-35.56, -0.13) * mm});
            skPoint(sketch, "E27.7.4", {"position": v(-35.35, 3.85) * mm});
            skLineSegment(sketch, "E27.7.5", {"start": v(-37.84, -0.01) * mm, "end": v(-36.04, -0.1) * mm});
            skPoint(sketch, "E27.7.6", {"position": v(-40.54, 2.81) * mm});
            skLineSegment(sketch, "E27.7.7", {"start": v(-37.63, 3.97) * mm, "end": v(-35.83, 3.87) * mm});
            skArc(sketch, "E27.7.8", {"start": v(-38.17, 3.9) * mm, "mid": v(-39.27, 3.5) * mm, "end": v(-40.3, 2.96) * mm});
            skPoint(sketch, "E27.7.9", {"position": v(-37.9, 3.98) * mm});
            skArc(sketch, "E27.7.10", {"start": v(-35.55, -0.6) * mm, "mid": v(-35.7, -0.26) * mm, "end": v(-36.04, -0.1) * mm});
            skArc(sketch, "E27.7.11", {"start": v(-35.83, 3.87) * mm, "mid": v(-35.47, 4) * mm, "end": v(-35.3, 4.32) * mm});
            skArc(sketch, "E27.7.12", {"start": v(-37.63, 3.97) * mm, "mid": v(-37.9, 3.96) * mm, "end": v(-38.17, 3.9) * mm});
            skArc(sketch, "E27.7.13", {"start": v(-40.6, 1.7) * mm, "mid": v(-40.55, 1.46) * mm, "end": v(-40.4, 1.27) * mm});
            skArc(sketch, "E27.7.14", {"start": v(-40.3, 2.96) * mm, "mid": v(-40.48, 2.78) * mm, "end": v(-40.56, 2.55) * mm});
            skArc(sketch, "E27.7.15", {"start": v(-38.37, 0.1) * mm, "mid": v(-38.1, 0.02) * mm, "end": v(-37.84, -0.01) * mm});
            skLineSegment(sketch, "E27.7.16", {"start": v(-40.6, 1.7) * mm, "end": v(-40.58, 2.13) * mm});
            skLineSegment(sketch, "E27.7.17", {"start": v(-40.56, 2.55) * mm, "end": v(-40.58, 2.13) * mm});
            skPoint(sketch, "E27.8.0", {"position": v(-40.03, -7.04) * mm});
            skPoint(sketch, "E27.8.1", {"position": v(-37.27, -7.92) * mm});
            skArc(sketch, "E27.8.2", {"start": v(-37.55, -7.87) * mm, "mid": v(-38.69, -7.58) * mm, "end": v(-39.78, -7.16) * mm});
            skPoint(sketch, "E27.8.3", {"position": v(-34.76, -7.52) * mm});
            skPoint(sketch, "E27.8.4", {"position": v(-35.38, -3.58) * mm});
            skLineSegment(sketch, "E27.8.5", {"start": v(-37, -7.88) * mm, "end": v(-35.23, -7.6) * mm});
            skPoint(sketch, "E27.8.6", {"position": v(-40.24, -5.68) * mm});
            skLineSegment(sketch, "E27.8.7", {"start": v(-37.63, -3.94) * mm, "end": v(-35.85, -3.66) * mm});
            skArc(sketch, "E27.8.8", {"start": v(-38.15, -4.12) * mm, "mid": v(-39.14, -4.74) * mm, "end": v(-40.04, -5.49) * mm});
            skPoint(sketch, "E27.8.9", {"position": v(-37.9, -3.98) * mm});
            skArc(sketch, "E27.8.10", {"start": v(-34.65, -7.99) * mm, "mid": v(-34.86, -7.68) * mm, "end": v(-35.23, -7.6) * mm});
            skArc(sketch, "E27.8.11", {"start": v(-35.85, -3.66) * mm, "mid": v(-35.53, -3.47) * mm, "end": v(-35.42, -3.11) * mm});
            skArc(sketch, "E27.8.12", {"start": v(-37.63, -3.94) * mm, "mid": v(-37.9, -4) * mm, "end": v(-38.15, -4.12) * mm});
            skArc(sketch, "E27.8.13", {"start": v(-40.07, -6.77) * mm, "mid": v(-39.97, -7) * mm, "end": v(-39.78, -7.16) * mm});
            skArc(sketch, "E27.8.14", {"start": v(-40.04, -5.49) * mm, "mid": v(-40.18, -5.7) * mm, "end": v(-40.2, -5.94) * mm});
            skArc(sketch, "E27.8.15", {"start": v(-37.55, -7.87) * mm, "mid": v(-37.28, -7.9) * mm, "end": v(-37, -7.88) * mm});
            skLineSegment(sketch, "E27.8.16", {"start": v(-40.07, -6.77) * mm, "end": v(-40.13, -6.36) * mm});
            skLineSegment(sketch, "E27.8.17", {"start": v(-40.2, -5.94) * mm, "end": v(-40.13, -6.36) * mm});
            skPoint(sketch, "E27.9.0", {"position": v(-37.69, -15.2) * mm});
            skPoint(sketch, "E27.9.1", {"position": v(-34.8, -15.5) * mm});
            skArc(sketch, "E27.9.2", {"start": v(-35.1, -15.5) * mm, "mid": v(-36.27, -15.46) * mm, "end": v(-37.42, -15.27) * mm});
            skPoint(sketch, "E27.9.3", {"position": v(-32.43, -14.59) * mm});
            skPoint(sketch, "E27.9.4", {"position": v(-33.86, -10.86) * mm});
            skLineSegment(sketch, "E27.9.5", {"start": v(-34.56, -15.4) * mm, "end": v(-32.88, -14.76) * mm});
            skPoint(sketch, "E27.9.6", {"position": v(-38.18, -13.92) * mm});
            skLineSegment(sketch, "E27.9.7", {"start": v(-35.99, -11.68) * mm, "end": v(-34.3, -11.03) * mm});
            skArc(sketch, "E27.9.8", {"start": v(-36.46, -11.96) * mm, "mid": v(-37.3, -12.78) * mm, "end": v(-38.03, -13.7) * mm});
            skPoint(sketch, "E27.9.9", {"position": v(-36.24, -11.77) * mm});
            skArc(sketch, "E27.9.10", {"start": v(-32.23, -15.02) * mm, "mid": v(-32.5, -14.76) * mm, "end": v(-32.88, -14.76) * mm});
            skArc(sketch, "E27.9.11", {"start": v(-34.3, -11.03) * mm, "mid": v(-34.03, -10.78) * mm, "end": v(-34, -10.4) * mm});
            skArc(sketch, "E27.9.12", {"start": v(-35.99, -11.68) * mm, "mid": v(-36.24, -11.8) * mm, "end": v(-36.46, -11.96) * mm});
            skArc(sketch, "E27.9.13", {"start": v(-37.78, -14.96) * mm, "mid": v(-37.64, -15.16) * mm, "end": v(-37.42, -15.27) * mm});
            skArc(sketch, "E27.9.14", {"start": v(-38.03, -13.7) * mm, "mid": v(-38.12, -13.92) * mm, "end": v(-38.09, -14.17) * mm});
            skArc(sketch, "E27.9.15", {"start": v(-35.1, -15.5) * mm, "mid": v(-34.82, -15.48) * mm, "end": v(-34.56, -15.4) * mm});
            skLineSegment(sketch, "E27.9.16", {"start": v(-37.78, -14.96) * mm, "end": v(-37.94, -14.56) * mm});
            skLineSegment(sketch, "E27.9.17", {"start": v(-38.09, -14.17) * mm, "end": v(-37.94, -14.56) * mm});
            skPoint(sketch, "E27.10.0", {"position": v(-33.7, -22.7) * mm});
            skPoint(sketch, "E27.10.1", {"position": v(-30.82, -22.4) * mm});
            skArc(sketch, "E27.10.2", {"start": v(-31.1, -22.46) * mm, "mid": v(-32.26, -22.66) * mm, "end": v(-33.43, -22.72) * mm});
            skPoint(sketch, "E27.10.3", {"position": v(-28.7, -21) * mm});
            skPoint(sketch, "E27.10.4", {"position": v(-30.86, -17.66) * mm});
            skLineSegment(sketch, "E27.10.5", {"start": v(-30.6, -22.25) * mm, "end": v(-29.1, -21.27) * mm});
            skPoint(sketch, "E27.10.6", {"position": v(-34.45, -21.55) * mm});
            skLineSegment(sketch, "E27.10.7", {"start": v(-32.77, -18.9) * mm, "end": v(-31.26, -17.92) * mm});
            skArc(sketch, "E27.10.8", {"start": v(-33.17, -19.28) * mm, "mid": v(-33.82, -20.25) * mm, "end": v(-34.35, -21.3) * mm});
            skPoint(sketch, "E27.10.9", {"position": v(-33, -19.05) * mm});
            skArc(sketch, "E27.10.10", {"start": v(-28.4, -21.39) * mm, "mid": v(-28.73, -21.2) * mm, "end": v(-29.1, -21.27) * mm});
            skArc(sketch, "E27.10.11", {"start": v(-31.26, -17.92) * mm, "mid": v(-31.05, -17.62) * mm, "end": v(-31.1, -17.25) * mm});
            skArc(sketch, "E27.10.12", {"start": v(-32.77, -18.9) * mm, "mid": v(-33, -19.07) * mm, "end": v(-33.17, -19.28) * mm});
            skArc(sketch, "E27.10.13", {"start": v(-33.85, -22.49) * mm, "mid": v(-33.67, -22.65) * mm, "end": v(-33.43, -22.72) * mm});
            skArc(sketch, "E27.10.14", {"start": v(-34.35, -21.3) * mm, "mid": v(-34.39, -21.54) * mm, "end": v(-34.3, -21.78) * mm});
            skArc(sketch, "E27.10.15", {"start": v(-31.1, -22.46) * mm, "mid": v(-30.84, -22.38) * mm, "end": v(-30.6, -22.25) * mm});
            skLineSegment(sketch, "E27.10.16", {"start": v(-33.85, -22.49) * mm, "end": v(-34.08, -22.13) * mm});
            skLineSegment(sketch, "E27.10.17", {"start": v(-34.3, -21.78) * mm, "end": v(-34.08, -22.13) * mm});
            skPoint(sketch, "E27.11.0", {"position": v(-28.25, -29.22) * mm});
            skPoint(sketch, "E27.11.1", {"position": v(-25.5, -28.31) * mm});
            skArc(sketch, "E27.11.2", {"start": v(-25.75, -28.44) * mm, "mid": v(-26.84, -28.87) * mm, "end": v(-27.98, -29.17) * mm});
            skPoint(sketch, "E27.11.3", {"position": v(-23.7, -26.52) * mm});
            skPoint(sketch, "E27.11.4", {"position": v(-26.52, -23.7) * mm});
            skLineSegment(sketch, "E27.11.5", {"start": v(-25.3, -28.13) * mm, "end": v(-24.03, -26.85) * mm});
            skPoint(sketch, "E27.11.6", {"position": v(-29.22, -28.25) * mm});
            skLineSegment(sketch, "E27.11.7", {"start": v(-28.13, -25.3) * mm, "end": v(-26.85, -24.03) * mm});
            skArc(sketch, "E27.11.8", {"start": v(-28.44, -25.75) * mm, "mid": v(-28.87, -26.84) * mm, "end": v(-29.17, -27.98) * mm});
            skPoint(sketch, "E27.11.9", {"position": v(-28.31, -25.5) * mm});
            skArc(sketch, "E27.11.10", {"start": v(-23.34, -26.83) * mm, "mid": v(-23.7, -26.7) * mm, "end": v(-24.03, -26.85) * mm});
            skArc(sketch, "E27.11.11", {"start": v(-26.85, -24.03) * mm, "mid": v(-26.7, -23.7) * mm, "end": v(-26.83, -23.34) * mm});
            skArc(sketch, "E27.11.12", {"start": v(-28.13, -25.3) * mm, "mid": v(-28.3, -25.52) * mm, "end": v(-28.44, -25.75) * mm});
            skArc(sketch, "E27.11.13", {"start": v(-28.43, -29.03) * mm, "mid": v(-28.22, -29.16) * mm, "end": v(-27.98, -29.17) * mm});
            skArc(sketch, "E27.11.14", {"start": v(-29.17, -27.98) * mm, "mid": v(-29.16, -28.22) * mm, "end": v(-29.03, -28.43) * mm});
            skArc(sketch, "E27.11.15", {"start": v(-25.75, -28.44) * mm, "mid": v(-25.52, -28.3) * mm, "end": v(-25.3, -28.13) * mm});
            skLineSegment(sketch, "E27.11.16", {"start": v(-28.43, -29.03) * mm, "end": v(-28.73, -28.73) * mm});
            skLineSegment(sketch, "E27.11.17", {"start": v(-29.03, -28.43) * mm, "end": v(-28.73, -28.73) * mm});
            skPoint(sketch, "E27.12.0", {"position": v(-21.55, -34.45) * mm});
            skPoint(sketch, "E27.12.1", {"position": v(-19.05, -33) * mm});
            skArc(sketch, "E27.12.2", {"start": v(-19.28, -33.17) * mm, "mid": v(-20.25, -33.82) * mm, "end": v(-21.3, -34.35) * mm});
            skPoint(sketch, "E27.12.3", {"position": v(-17.66, -30.86) * mm});
            skPoint(sketch, "E27.12.4", {"position": v(-21, -28.7) * mm});
            skLineSegment(sketch, "E27.12.5", {"start": v(-18.9, -32.77) * mm, "end": v(-17.92, -31.26) * mm});
            skPoint(sketch, "E27.12.6", {"position": v(-22.7, -33.7) * mm});
            skLineSegment(sketch, "E27.12.7", {"start": v(-22.25, -30.6) * mm, "end": v(-21.27, -29.1) * mm});
            skArc(sketch, "E27.12.8", {"start": v(-22.46, -31.1) * mm, "mid": v(-22.66, -32.26) * mm, "end": v(-22.72, -33.43) * mm});
            skPoint(sketch, "E27.12.9", {"position": v(-22.4, -30.82) * mm});
            skArc(sketch, "E27.12.10", {"start": v(-17.25, -31.1) * mm, "mid": v(-17.62, -31.05) * mm, "end": v(-17.92, -31.26) * mm});
            skArc(sketch, "E27.12.11", {"start": v(-21.27, -29.1) * mm, "mid": v(-21.2, -28.73) * mm, "end": v(-21.39, -28.4) * mm});
            skArc(sketch, "E27.12.12", {"start": v(-22.25, -30.6) * mm, "mid": v(-22.38, -30.84) * mm, "end": v(-22.46, -31.1) * mm});
            skArc(sketch, "E27.12.13", {"start": v(-21.78, -34.3) * mm, "mid": v(-21.54, -34.39) * mm, "end": v(-21.3, -34.35) * mm});
            skArc(sketch, "E27.12.14", {"start": v(-22.72, -33.43) * mm, "mid": v(-22.65, -33.67) * mm, "end": v(-22.49, -33.85) * mm});
            skArc(sketch, "E27.12.15", {"start": v(-19.28, -33.17) * mm, "mid": v(-19.07, -33) * mm, "end": v(-18.9, -32.77) * mm});
            skLineSegment(sketch, "E27.12.16", {"start": v(-21.78, -34.3) * mm, "end": v(-22.13, -34.08) * mm});
            skLineSegment(sketch, "E27.12.17", {"start": v(-22.49, -33.85) * mm, "end": v(-22.13, -34.08) * mm});
            skPoint(sketch, "E27.13.0", {"position": v(-13.92, -38.18) * mm});
            skPoint(sketch, "E27.13.1", {"position": v(-11.77, -36.24) * mm});
            skArc(sketch, "E27.13.2", {"start": v(-11.96, -36.46) * mm, "mid": v(-12.78, -37.3) * mm, "end": v(-13.7, -38.03) * mm});
            skPoint(sketch, "E27.13.3", {"position": v(-10.86, -33.86) * mm});
            skPoint(sketch, "E27.13.4", {"position": v(-14.59, -32.43) * mm});
            skLineSegment(sketch, "E27.13.5", {"start": v(-11.68, -35.99) * mm, "end": v(-11.03, -34.3) * mm});
            skPoint(sketch, "E27.13.6", {"position": v(-15.2, -37.69) * mm});
            skLineSegment(sketch, "E27.13.7", {"start": v(-15.4, -34.56) * mm, "end": v(-14.76, -32.88) * mm});
            skArc(sketch, "E27.13.8", {"start": v(-15.5, -35.1) * mm, "mid": v(-15.46, -36.27) * mm, "end": v(-15.27, -37.42) * mm});
            skPoint(sketch, "E27.13.9", {"position": v(-15.5, -34.8) * mm});
            skArc(sketch, "E27.13.10", {"start": v(-10.4, -34) * mm, "mid": v(-10.78, -34.03) * mm, "end": v(-11.03, -34.3) * mm});
            skArc(sketch, "E27.13.11", {"start": v(-14.76, -32.88) * mm, "mid": v(-14.76, -32.5) * mm, "end": v(-15.02, -32.23) * mm});
            skArc(sketch, "E27.13.12", {"start": v(-15.4, -34.56) * mm, "mid": v(-15.48, -34.82) * mm, "end": v(-15.5, -35.1) * mm});
            skArc(sketch, "E27.13.13", {"start": v(-14.17, -38.09) * mm, "mid": v(-13.92, -38.12) * mm, "end": v(-13.7, -38.03) * mm});
            skArc(sketch, "E27.13.14", {"start": v(-15.27, -37.42) * mm, "mid": v(-15.16, -37.64) * mm, "end": v(-14.96, -37.78) * mm});
            skArc(sketch, "E27.13.15", {"start": v(-11.96, -36.46) * mm, "mid": v(-11.8, -36.24) * mm, "end": v(-11.68, -35.99) * mm});
            skLineSegment(sketch, "E27.13.16", {"start": v(-14.17, -38.09) * mm, "end": v(-14.56, -37.94) * mm});
            skLineSegment(sketch, "E27.13.17", {"start": v(-14.96, -37.78) * mm, "end": v(-14.56, -37.94) * mm});
            skPoint(sketch, "E27.14.0", {"position": v(-5.68, -40.24) * mm});
            skPoint(sketch, "E27.14.1", {"position": v(-3.98, -37.9) * mm});
            skArc(sketch, "E27.14.2", {"start": v(-4.12, -38.15) * mm, "mid": v(-4.74, -39.14) * mm, "end": v(-5.49, -40.04) * mm});
            skPoint(sketch, "E27.14.3", {"position": v(-3.58, -35.38) * mm});
            skPoint(sketch, "E27.14.4", {"position": v(-7.52, -34.76) * mm});
            skLineSegment(sketch, "E27.14.5", {"start": v(-3.94, -37.63) * mm, "end": v(-3.66, -35.85) * mm});
            skPoint(sketch, "E27.14.6", {"position": v(-7.04, -40.03) * mm});
            skLineSegment(sketch, "E27.14.7", {"start": v(-7.88, -37) * mm, "end": v(-7.6, -35.23) * mm});
            skArc(sketch, "E27.14.8", {"start": v(-7.87, -37.55) * mm, "mid": v(-7.58, -38.69) * mm, "end": v(-7.16, -39.78) * mm});
            skPoint(sketch, "E27.14.9", {"position": v(-7.92, -37.27) * mm});
            skArc(sketch, "E27.14.10", {"start": v(-3.11, -35.42) * mm, "mid": v(-3.47, -35.53) * mm, "end": v(-3.66, -35.85) * mm});
            skArc(sketch, "E27.14.11", {"start": v(-7.6, -35.23) * mm, "mid": v(-7.68, -34.86) * mm, "end": v(-7.99, -34.65) * mm});
            skArc(sketch, "E27.14.12", {"start": v(-7.88, -37) * mm, "mid": v(-7.9, -37.28) * mm, "end": v(-7.87, -37.55) * mm});
            skArc(sketch, "E27.14.13", {"start": v(-5.94, -40.2) * mm, "mid": v(-5.7, -40.18) * mm, "end": v(-5.49, -40.04) * mm});
            skArc(sketch, "E27.14.14", {"start": v(-7.16, -39.78) * mm, "mid": v(-7, -39.97) * mm, "end": v(-6.77, -40.07) * mm});
            skArc(sketch, "E27.14.15", {"start": v(-4.12, -38.15) * mm, "mid": v(-4, -37.9) * mm, "end": v(-3.94, -37.63) * mm});
            skLineSegment(sketch, "E27.14.16", {"start": v(-5.94, -40.2) * mm, "end": v(-6.36, -40.13) * mm});
            skLineSegment(sketch, "E27.14.17", {"start": v(-6.77, -40.07) * mm, "end": v(-6.36, -40.13) * mm});
            skPoint(sketch, "E27.15.0", {"position": v(2.81, -40.54) * mm});
            skPoint(sketch, "E27.15.1", {"position": v(3.98, -37.9) * mm});
            skArc(sketch, "E27.15.2", {"start": v(3.9, -38.17) * mm, "mid": v(3.5, -39.27) * mm, "end": v(2.96, -40.3) * mm});
            skPoint(sketch, "E27.15.3", {"position": v(3.85, -35.35) * mm});
            skPoint(sketch, "E27.15.4", {"position": v(-0.13, -35.56) * mm});
            skLineSegment(sketch, "E27.15.5", {"start": v(3.97, -37.63) * mm, "end": v(3.87, -35.83) * mm});
            skPoint(sketch, "E27.15.6", {"position": v(1.44, -40.61) * mm});
            skLineSegment(sketch, "E27.15.7", {"start": v(-0.01, -37.84) * mm, "end": v(-0.1, -36.04) * mm});
            skArc(sketch, "E27.15.8", {"start": v(0.1, -38.37) * mm, "mid": v(0.63, -39.42) * mm, "end": v(1.27, -40.4) * mm});
            skPoint(sketch, "E27.15.9", {"position": v(0, -38.1) * mm});
            skArc(sketch, "E27.15.10", {"start": v(4.32, -35.3) * mm, "mid": v(4, -35.47) * mm, "end": v(3.87, -35.83) * mm});
            skArc(sketch, "E27.15.11", {"start": v(-0.1, -36.04) * mm, "mid": v(-0.26, -35.7) * mm, "end": v(-0.6, -35.55) * mm});
            skArc(sketch, "E27.15.12", {"start": v(-0.01, -37.84) * mm, "mid": v(0.02, -38.1) * mm, "end": v(0.1, -38.37) * mm});
            skArc(sketch, "E27.15.13", {"start": v(2.55, -40.56) * mm, "mid": v(2.78, -40.48) * mm, "end": v(2.96, -40.3) * mm});
            skArc(sketch, "E27.15.14", {"start": v(1.27, -40.4) * mm, "mid": v(1.46, -40.55) * mm, "end": v(1.7, -40.6) * mm});
            skArc(sketch, "E27.15.15", {"start": v(3.9, -38.17) * mm, "mid": v(3.96, -37.9) * mm, "end": v(3.97, -37.63) * mm});
            skLineSegment(sketch, "E27.15.16", {"start": v(2.55, -40.56) * mm, "end": v(2.13, -40.58) * mm});
            skLineSegment(sketch, "E27.15.17", {"start": v(1.7, -40.6) * mm, "end": v(2.13, -40.58) * mm});
            skPoint(sketch, "E27.16.0", {"position": v(11.18, -39.07) * mm});
            skPoint(sketch, "E27.16.1", {"position": v(11.77, -36.24) * mm});
            skArc(sketch, "E27.16.2", {"start": v(11.75, -36.52) * mm, "mid": v(11.58, -37.68) * mm, "end": v(11.27, -38.81) * mm});
            skPoint(sketch, "E27.16.3", {"position": v(11.12, -33.78) * mm});
            skPoint(sketch, "E27.16.4", {"position": v(7.26, -34.81) * mm});
            skLineSegment(sketch, "E27.16.5", {"start": v(11.7, -35.98) * mm, "end": v(11.24, -34.24) * mm});
            skPoint(sketch, "E27.16.6", {"position": v(9.85, -39.43) * mm});
            skLineSegment(sketch, "E27.16.7", {"start": v(7.85, -37.01) * mm, "end": v(7.39, -35.27) * mm});
            skArc(sketch, "E27.16.8", {"start": v(8.08, -37.5) * mm, "mid": v(8.8, -38.43) * mm, "end": v(9.64, -39.25) * mm});
            skPoint(sketch, "E27.16.9", {"position": v(7.92, -37.27) * mm});
            skArc(sketch, "E27.16.10", {"start": v(11.56, -33.63) * mm, "mid": v(11.28, -33.87) * mm, "end": v(11.24, -34.24) * mm});
            skArc(sketch, "E27.16.11", {"start": v(7.39, -35.27) * mm, "mid": v(7.16, -34.97) * mm, "end": v(6.8, -34.9) * mm});
            skArc(sketch, "E27.16.12", {"start": v(7.85, -37.01) * mm, "mid": v(7.95, -37.27) * mm, "end": v(8.08, -37.5) * mm});
            skArc(sketch, "E27.16.13", {"start": v(10.92, -39.14) * mm, "mid": v(11.14, -39.02) * mm, "end": v(11.27, -38.81) * mm});
            skArc(sketch, "E27.16.14", {"start": v(9.64, -39.25) * mm, "mid": v(9.86, -39.36) * mm, "end": v(10.1, -39.36) * mm});
            skArc(sketch, "E27.16.15", {"start": v(11.75, -36.52) * mm, "mid": v(11.75, -36.25) * mm, "end": v(11.7, -35.98) * mm});
            skLineSegment(sketch, "E27.16.16", {"start": v(10.92, -39.14) * mm, "end": v(10.52, -39.25) * mm});
            skLineSegment(sketch, "E27.16.17", {"start": v(10.1, -39.36) * mm, "end": v(10.52, -39.25) * mm});
            skPoint(sketch, "E27.17.0", {"position": v(19.06, -35.9) * mm});
            skPoint(sketch, "E27.17.1", {"position": v(19.05, -33) * mm});
            skArc(sketch, "E27.17.2", {"start": v(19.1, -33.28) * mm, "mid": v(19.17, -34.45) * mm, "end": v(19.1, -35.62) * mm});
            skPoint(sketch, "E27.17.3", {"position": v(17.9, -30.73) * mm});
            skPoint(sketch, "E27.17.4", {"position": v(14.34, -32.54) * mm});
            skLineSegment(sketch, "E27.17.5", {"start": v(18.93, -32.76) * mm, "end": v(18.11, -31.15) * mm});
            skPoint(sketch, "E27.17.6", {"position": v(17.83, -36.52) * mm});
            skLineSegment(sketch, "E27.17.7", {"start": v(15.38, -34.57) * mm, "end": v(14.56, -32.96) * mm});
            skArc(sketch, "E27.17.8", {"start": v(15.7, -35) * mm, "mid": v(16.6, -35.76) * mm, "end": v(17.6, -36.39) * mm});
            skPoint(sketch, "E27.17.9", {"position": v(15.5, -34.8) * mm});
            skArc(sketch, "E27.17.10", {"start": v(18.3, -30.49) * mm, "mid": v(18.08, -30.78) * mm, "end": v(18.11, -31.15) * mm});
            skArc(sketch, "E27.17.11", {"start": v(14.56, -32.96) * mm, "mid": v(14.28, -32.72) * mm, "end": v(13.9, -32.73) * mm});
            skArc(sketch, "E27.17.12", {"start": v(15.38, -34.57) * mm, "mid": v(15.52, -34.8) * mm, "end": v(15.7, -35) * mm});
            skArc(sketch, "E27.17.13", {"start": v(18.82, -36.01) * mm, "mid": v(19, -35.85) * mm, "end": v(19.1, -35.62) * mm});
            skArc(sketch, "E27.17.14", {"start": v(17.6, -36.39) * mm, "mid": v(17.83, -36.45) * mm, "end": v(18.07, -36.4) * mm});
            skArc(sketch, "E27.17.15", {"start": v(19.1, -33.28) * mm, "mid": v(19.03, -33.01) * mm, "end": v(18.93, -32.76) * mm});
            skLineSegment(sketch, "E27.17.16", {"start": v(18.82, -36.01) * mm, "end": v(18.45, -36.2) * mm});
            skLineSegment(sketch, "E27.17.17", {"start": v(18.07, -36.4) * mm, "end": v(18.45, -36.2) * mm});
            skPoint(sketch, "E27.18.0", {"position": v(26.1, -31.15) * mm});
            skPoint(sketch, "E27.18.1", {"position": v(25.5, -28.31) * mm});
            skArc(sketch, "E27.18.2", {"start": v(25.6, -28.59) * mm, "mid": v(25.91, -29.71) * mm, "end": v(26.09, -30.87) * mm});
            skPoint(sketch, "E27.18.3", {"position": v(23.9, -26.34) * mm});
            skPoint(sketch, "E27.18.4", {"position": v(20.8, -28.85) * mm});
            skLineSegment(sketch, "E27.18.5", {"start": v(25.33, -28.1) * mm, "end": v(24.2, -26.7) * mm});
            skPoint(sketch, "E27.18.6", {"position": v(25.04, -32.01) * mm});
            skLineSegment(sketch, "E27.18.7", {"start": v(22.23, -30.62) * mm, "end": v(21.1, -29.22) * mm});
            skArc(sketch, "E27.18.8", {"start": v(22.64, -30.98) * mm, "mid": v(23.68, -31.52) * mm, "end": v(24.77, -31.94) * mm});
            skPoint(sketch, "E27.18.9", {"position": v(22.4, -30.82) * mm});
            skArc(sketch, "E27.18.10", {"start": v(24.24, -26.02) * mm, "mid": v(24.08, -26.35) * mm, "end": v(24.2, -26.7) * mm});
            skArc(sketch, "E27.18.11", {"start": v(21.1, -29.22) * mm, "mid": v(20.77, -29.03) * mm, "end": v(20.4, -29.12) * mm});
            skArc(sketch, "E27.18.12", {"start": v(22.23, -30.62) * mm, "mid": v(22.42, -30.82) * mm, "end": v(22.64, -30.98) * mm});
            skArc(sketch, "E27.18.13", {"start": v(25.9, -31.31) * mm, "mid": v(26.05, -31.12) * mm, "end": v(26.09, -30.87) * mm});
            skArc(sketch, "E27.18.14", {"start": v(24.77, -31.94) * mm, "mid": v(25.02, -31.95) * mm, "end": v(25.24, -31.84) * mm});
            skArc(sketch, "E27.18.15", {"start": v(25.6, -28.59) * mm, "mid": v(25.48, -28.34) * mm, "end": v(25.33, -28.1) * mm});
            skLineSegment(sketch, "E27.18.16", {"start": v(25.9, -31.31) * mm, "end": v(25.57, -31.58) * mm});
            skLineSegment(sketch, "E27.18.17", {"start": v(25.24, -31.84) * mm, "end": v(25.57, -31.58) * mm});
            skPoint(sketch, "E27.19.0", {"position": v(32.01, -25.04) * mm});
            skPoint(sketch, "E27.19.1", {"position": v(30.82, -22.4) * mm});
            skArc(sketch, "E27.19.2", {"start": v(30.98, -22.64) * mm, "mid": v(31.52, -23.68) * mm, "end": v(31.94, -24.77) * mm});
            skPoint(sketch, "E27.19.3", {"position": v(28.85, -20.8) * mm});
            skPoint(sketch, "E27.19.4", {"position": v(26.34, -23.9) * mm});
            skLineSegment(sketch, "E27.19.5", {"start": v(30.62, -22.23) * mm, "end": v(29.22, -21.1) * mm});
            skPoint(sketch, "E27.19.6", {"position": v(31.15, -26.1) * mm});
            skLineSegment(sketch, "E27.19.7", {"start": v(28.1, -25.33) * mm, "end": v(26.7, -24.2) * mm});
            skArc(sketch, "E27.19.8", {"start": v(28.59, -25.6) * mm, "mid": v(29.71, -25.91) * mm, "end": v(30.87, -26.09) * mm});
            skPoint(sketch, "E27.19.9", {"position": v(28.31, -25.5) * mm});
            skArc(sketch, "E27.19.10", {"start": v(29.12, -20.4) * mm, "mid": v(29.03, -20.77) * mm, "end": v(29.22, -21.1) * mm});
            skArc(sketch, "E27.19.11", {"start": v(26.7, -24.2) * mm, "mid": v(26.35, -24.08) * mm, "end": v(26.02, -24.24) * mm});
            skArc(sketch, "E27.19.12", {"start": v(28.1, -25.33) * mm, "mid": v(28.34, -25.48) * mm, "end": v(28.59, -25.6) * mm});
            skArc(sketch, "E27.19.13", {"start": v(31.84, -25.24) * mm, "mid": v(31.95, -25.02) * mm, "end": v(31.94, -24.77) * mm});
            skArc(sketch, "E27.19.14", {"start": v(30.87, -26.09) * mm, "mid": v(31.12, -26.05) * mm, "end": v(31.31, -25.9) * mm});
            skArc(sketch, "E27.19.15", {"start": v(30.98, -22.64) * mm, "mid": v(30.82, -22.42) * mm, "end": v(30.62, -22.23) * mm});
            skLineSegment(sketch, "E27.19.16", {"start": v(31.84, -25.24) * mm, "end": v(31.58, -25.57) * mm});
            skLineSegment(sketch, "E27.19.17", {"start": v(31.31, -25.9) * mm, "end": v(31.58, -25.57) * mm});
            skPoint(sketch, "E27.20.0", {"position": v(36.52, -17.83) * mm});
            skPoint(sketch, "E27.20.1", {"position": v(34.8, -15.5) * mm});
            skArc(sketch, "E27.20.2", {"start": v(35, -15.7) * mm, "mid": v(35.76, -16.6) * mm, "end": v(36.39, -17.6) * mm});
            skPoint(sketch, "E27.20.3", {"position": v(32.54, -14.34) * mm});
            skPoint(sketch, "E27.20.4", {"position": v(30.73, -17.9) * mm});
            skLineSegment(sketch, "E27.20.5", {"start": v(34.57, -15.38) * mm, "end": v(32.96, -14.56) * mm});
            skPoint(sketch, "E27.20.6", {"position": v(35.9, -19.06) * mm});
            skLineSegment(sketch, "E27.20.7", {"start": v(32.76, -18.93) * mm, "end": v(31.15, -18.11) * mm});
            skArc(sketch, "E27.20.8", {"start": v(33.28, -19.1) * mm, "mid": v(34.45, -19.17) * mm, "end": v(35.62, -19.1) * mm});
            skPoint(sketch, "E27.20.9", {"position": v(33, -19.05) * mm});
            skArc(sketch, "E27.20.10", {"start": v(32.73, -13.9) * mm, "mid": v(32.72, -14.28) * mm, "end": v(32.96, -14.56) * mm});
            skArc(sketch, "E27.20.11", {"start": v(31.15, -18.11) * mm, "mid": v(30.78, -18.08) * mm, "end": v(30.49, -18.3) * mm});
            skArc(sketch, "E27.20.12", {"start": v(32.76, -18.93) * mm, "mid": v(33.01, -19.03) * mm, "end": v(33.28, -19.1) * mm});
            skArc(sketch, "E27.20.13", {"start": v(36.4, -18.07) * mm, "mid": v(36.45, -17.83) * mm, "end": v(36.39, -17.6) * mm});
            skArc(sketch, "E27.20.14", {"start": v(35.62, -19.1) * mm, "mid": v(35.85, -19) * mm, "end": v(36.01, -18.82) * mm});
            skArc(sketch, "E27.20.15", {"start": v(35, -15.7) * mm, "mid": v(34.8, -15.52) * mm, "end": v(34.57, -15.38) * mm});
            skLineSegment(sketch, "E27.20.16", {"start": v(36.4, -18.07) * mm, "end": v(36.2, -18.45) * mm});
            skLineSegment(sketch, "E27.20.17", {"start": v(36.01, -18.82) * mm, "end": v(36.2, -18.45) * mm});
            skPoint(sketch, "E27.21.0", {"position": v(39.43, -9.85) * mm});
            skPoint(sketch, "E27.21.1", {"position": v(37.27, -7.92) * mm});
            skArc(sketch, "E27.21.2", {"start": v(37.5, -8.08) * mm, "mid": v(38.43, -8.8) * mm, "end": v(39.25, -9.64) * mm});
            skPoint(sketch, "E27.21.3", {"position": v(34.81, -7.26) * mm});
            skPoint(sketch, "E27.21.4", {"position": v(33.78, -11.12) * mm});
            skLineSegment(sketch, "E27.21.5", {"start": v(37.01, -7.85) * mm, "end": v(35.27, -7.39) * mm});
            skPoint(sketch, "E27.21.6", {"position": v(39.07, -11.18) * mm});
            skLineSegment(sketch, "E27.21.7", {"start": v(35.98, -11.7) * mm, "end": v(34.24, -11.24) * mm});
            skArc(sketch, "E27.21.8", {"start": v(36.52, -11.75) * mm, "mid": v(37.68, -11.58) * mm, "end": v(38.81, -11.27) * mm});
            skPoint(sketch, "E27.21.9", {"position": v(36.24, -11.77) * mm});
            skArc(sketch, "E27.21.10", {"start": v(34.9, -6.8) * mm, "mid": v(34.97, -7.16) * mm, "end": v(35.27, -7.39) * mm});
            skArc(sketch, "E27.21.11", {"start": v(34.24, -11.24) * mm, "mid": v(33.87, -11.28) * mm, "end": v(33.63, -11.56) * mm});
            skArc(sketch, "E27.21.12", {"start": v(35.98, -11.7) * mm, "mid": v(36.25, -11.75) * mm, "end": v(36.52, -11.75) * mm});
            skArc(sketch, "E27.21.13", {"start": v(39.36, -10.1) * mm, "mid": v(39.36, -9.86) * mm, "end": v(39.25, -9.64) * mm});
            skArc(sketch, "E27.21.14", {"start": v(38.81, -11.27) * mm, "mid": v(39.02, -11.14) * mm, "end": v(39.14, -10.92) * mm});
            skArc(sketch, "E27.21.15", {"start": v(37.5, -8.08) * mm, "mid": v(37.27, -7.95) * mm, "end": v(37.01, -7.85) * mm});
            skLineSegment(sketch, "E27.21.16", {"start": v(39.36, -10.1) * mm, "end": v(39.25, -10.52) * mm});
            skLineSegment(sketch, "E27.21.17", {"start": v(39.14, -10.92) * mm, "end": v(39.25, -10.52) * mm});
            skPoint(sketch, "E27.22.0", {"position": v(40.61, -1.44) * mm});
            skPoint(sketch, "E27.22.1", {"position": v(38.1, 0) * mm});
            skArc(sketch, "E27.22.2", {"start": v(38.37, -0.1) * mm, "mid": v(39.42, -0.63) * mm, "end": v(40.4, -1.27) * mm});
            skPoint(sketch, "E27.22.3", {"position": v(35.56, 0.13) * mm});
            skPoint(sketch, "E27.22.4", {"position": v(35.35, -3.85) * mm});
            skLineSegment(sketch, "E27.22.5", {"start": v(37.84, 0.01) * mm, "end": v(36.04, 0.1) * mm});
            skPoint(sketch, "E27.22.6", {"position": v(40.54, -2.81) * mm});
            skLineSegment(sketch, "E27.22.7", {"start": v(37.63, -3.97) * mm, "end": v(35.83, -3.87) * mm});
            skArc(sketch, "E27.22.8", {"start": v(38.17, -3.9) * mm, "mid": v(39.27, -3.5) * mm, "end": v(40.3, -2.96) * mm});
            skPoint(sketch, "E27.22.9", {"position": v(37.9, -3.98) * mm});
            skArc(sketch, "E27.22.10", {"start": v(35.55, 0.6) * mm, "mid": v(35.7, 0.26) * mm, "end": v(36.04, 0.1) * mm});
            skArc(sketch, "E27.22.11", {"start": v(35.83, -3.87) * mm, "mid": v(35.47, -4) * mm, "end": v(35.3, -4.32) * mm});
            skArc(sketch, "E27.22.12", {"start": v(37.63, -3.97) * mm, "mid": v(37.9, -3.96) * mm, "end": v(38.17, -3.9) * mm});
            skArc(sketch, "E27.22.13", {"start": v(40.6, -1.7) * mm, "mid": v(40.55, -1.46) * mm, "end": v(40.4, -1.27) * mm});
            skArc(sketch, "E27.22.14", {"start": v(40.3, -2.96) * mm, "mid": v(40.48, -2.78) * mm, "end": v(40.56, -2.55) * mm});
            skArc(sketch, "E27.22.15", {"start": v(38.37, -0.1) * mm, "mid": v(38.1, -0.02) * mm, "end": v(37.84, 0.01) * mm});
            skLineSegment(sketch, "E27.22.16", {"start": v(40.6, -1.7) * mm, "end": v(40.58, -2.13) * mm});
            skLineSegment(sketch, "E27.22.17", {"start": v(40.56, -2.55) * mm, "end": v(40.58, -2.13) * mm});
            skPoint(sketch, "E27.23.0", {"position": v(40.03, 7.04) * mm});
            skPoint(sketch, "E27.23.1", {"position": v(37.27, 7.92) * mm});
            skArc(sketch, "E27.23.2", {"start": v(37.55, 7.87) * mm, "mid": v(38.69, 7.58) * mm, "end": v(39.78, 7.16) * mm});
            skPoint(sketch, "E27.23.3", {"position": v(34.76, 7.52) * mm});
            skPoint(sketch, "E27.23.4", {"position": v(35.38, 3.58) * mm});
            skLineSegment(sketch, "E27.23.5", {"start": v(37, 7.88) * mm, "end": v(35.23, 7.6) * mm});
            skPoint(sketch, "E27.23.6", {"position": v(40.24, 5.68) * mm});
            skLineSegment(sketch, "E27.23.7", {"start": v(37.63, 3.94) * mm, "end": v(35.85, 3.66) * mm});
            skArc(sketch, "E27.23.8", {"start": v(38.15, 4.12) * mm, "mid": v(39.14, 4.74) * mm, "end": v(40.04, 5.49) * mm});
            skPoint(sketch, "E27.23.9", {"position": v(37.9, 3.98) * mm});
            skArc(sketch, "E27.23.10", {"start": v(34.65, 7.99) * mm, "mid": v(34.86, 7.68) * mm, "end": v(35.23, 7.6) * mm});
            skArc(sketch, "E27.23.11", {"start": v(35.85, 3.66) * mm, "mid": v(35.53, 3.47) * mm, "end": v(35.42, 3.11) * mm});
            skArc(sketch, "E27.23.12", {"start": v(37.63, 3.94) * mm, "mid": v(37.9, 4) * mm, "end": v(38.15, 4.12) * mm});
            skArc(sketch, "E27.23.13", {"start": v(40.07, 6.77) * mm, "mid": v(39.97, 7) * mm, "end": v(39.78, 7.16) * mm});
            skArc(sketch, "E27.23.14", {"start": v(40.04, 5.49) * mm, "mid": v(40.18, 5.7) * mm, "end": v(40.2, 5.94) * mm});
            skArc(sketch, "E27.23.15", {"start": v(37.55, 7.87) * mm, "mid": v(37.28, 7.9) * mm, "end": v(37, 7.88) * mm});
            skLineSegment(sketch, "E27.23.16", {"start": v(40.07, 6.77) * mm, "end": v(40.13, 6.36) * mm});
            skLineSegment(sketch, "E27.23.17", {"start": v(40.2, 5.94) * mm, "end": v(40.13, 6.36) * mm});
            skPoint(sketch, "E27.24.0", {"position": v(37.69, 15.2) * mm});
            skPoint(sketch, "E27.24.1", {"position": v(34.8, 15.5) * mm});
            skArc(sketch, "E27.24.2", {"start": v(35.1, 15.5) * mm, "mid": v(36.27, 15.46) * mm, "end": v(37.42, 15.27) * mm});
            skPoint(sketch, "E27.24.3", {"position": v(32.43, 14.59) * mm});
            skPoint(sketch, "E27.24.4", {"position": v(33.86, 10.86) * mm});
            skLineSegment(sketch, "E27.24.5", {"start": v(34.56, 15.4) * mm, "end": v(32.88, 14.76) * mm});
            skPoint(sketch, "E27.24.6", {"position": v(38.18, 13.92) * mm});
            skLineSegment(sketch, "E27.24.7", {"start": v(35.99, 11.68) * mm, "end": v(34.3, 11.03) * mm});
            skArc(sketch, "E27.24.8", {"start": v(36.46, 11.96) * mm, "mid": v(37.3, 12.78) * mm, "end": v(38.03, 13.7) * mm});
            skPoint(sketch, "E27.24.9", {"position": v(36.24, 11.77) * mm});
            skArc(sketch, "E27.24.10", {"start": v(32.23, 15.02) * mm, "mid": v(32.5, 14.76) * mm, "end": v(32.88, 14.76) * mm});
            skArc(sketch, "E27.24.11", {"start": v(34.3, 11.03) * mm, "mid": v(34.03, 10.78) * mm, "end": v(34, 10.4) * mm});
            skArc(sketch, "E27.24.12", {"start": v(35.99, 11.68) * mm, "mid": v(36.24, 11.8) * mm, "end": v(36.46, 11.96) * mm});
            skArc(sketch, "E27.24.13", {"start": v(37.78, 14.96) * mm, "mid": v(37.64, 15.16) * mm, "end": v(37.42, 15.27) * mm});
            skArc(sketch, "E27.24.14", {"start": v(38.03, 13.7) * mm, "mid": v(38.12, 13.92) * mm, "end": v(38.09, 14.17) * mm});
            skArc(sketch, "E27.24.15", {"start": v(35.1, 15.5) * mm, "mid": v(34.82, 15.48) * mm, "end": v(34.56, 15.4) * mm});
            skLineSegment(sketch, "E27.24.16", {"start": v(37.78, 14.96) * mm, "end": v(37.94, 14.56) * mm});
            skLineSegment(sketch, "E27.24.17", {"start": v(38.09, 14.17) * mm, "end": v(37.94, 14.56) * mm});
            skPoint(sketch, "E27.25.0", {"position": v(33.7, 22.7) * mm});
            skPoint(sketch, "E27.25.1", {"position": v(30.82, 22.4) * mm});
            skArc(sketch, "E27.25.2", {"start": v(31.1, 22.46) * mm, "mid": v(32.26, 22.66) * mm, "end": v(33.43, 22.72) * mm});
            skPoint(sketch, "E27.25.3", {"position": v(28.7, 21) * mm});
            skPoint(sketch, "E27.25.4", {"position": v(30.86, 17.66) * mm});
            skLineSegment(sketch, "E27.25.5", {"start": v(30.6, 22.25) * mm, "end": v(29.1, 21.27) * mm});
            skPoint(sketch, "E27.25.6", {"position": v(34.45, 21.55) * mm});
            skLineSegment(sketch, "E27.25.7", {"start": v(32.77, 18.9) * mm, "end": v(31.26, 17.92) * mm});
            skArc(sketch, "E27.25.8", {"start": v(33.17, 19.28) * mm, "mid": v(33.82, 20.25) * mm, "end": v(34.35, 21.3) * mm});
            skPoint(sketch, "E27.25.9", {"position": v(33, 19.05) * mm});
            skArc(sketch, "E27.25.10", {"start": v(28.4, 21.39) * mm, "mid": v(28.73, 21.2) * mm, "end": v(29.1, 21.27) * mm});
            skArc(sketch, "E27.25.11", {"start": v(31.26, 17.92) * mm, "mid": v(31.05, 17.62) * mm, "end": v(31.1, 17.25) * mm});
            skArc(sketch, "E27.25.12", {"start": v(32.77, 18.9) * mm, "mid": v(33, 19.07) * mm, "end": v(33.17, 19.28) * mm});
            skArc(sketch, "E27.25.13", {"start": v(33.85, 22.49) * mm, "mid": v(33.67, 22.65) * mm, "end": v(33.43, 22.72) * mm});
            skArc(sketch, "E27.25.14", {"start": v(34.35, 21.3) * mm, "mid": v(34.39, 21.54) * mm, "end": v(34.3, 21.78) * mm});
            skArc(sketch, "E27.25.15", {"start": v(31.1, 22.46) * mm, "mid": v(30.84, 22.38) * mm, "end": v(30.6, 22.25) * mm});
            skLineSegment(sketch, "E27.25.16", {"start": v(33.85, 22.49) * mm, "end": v(34.08, 22.13) * mm});
            skLineSegment(sketch, "E27.25.17", {"start": v(34.3, 21.78) * mm, "end": v(34.08, 22.13) * mm});
            skPoint(sketch, "E27.26.0", {"position": v(28.25, 29.22) * mm});
            skPoint(sketch, "E27.26.1", {"position": v(25.5, 28.31) * mm});
            skArc(sketch, "E27.26.2", {"start": v(25.75, 28.44) * mm, "mid": v(26.84, 28.87) * mm, "end": v(27.98, 29.17) * mm});
            skPoint(sketch, "E27.26.3", {"position": v(23.7, 26.52) * mm});
            skPoint(sketch, "E27.26.4", {"position": v(26.52, 23.7) * mm});
            skLineSegment(sketch, "E27.26.5", {"start": v(25.3, 28.13) * mm, "end": v(24.03, 26.85) * mm});
            skPoint(sketch, "E27.26.6", {"position": v(29.22, 28.25) * mm});
            skLineSegment(sketch, "E27.26.7", {"start": v(28.13, 25.3) * mm, "end": v(26.85, 24.03) * mm});
            skArc(sketch, "E27.26.8", {"start": v(28.44, 25.75) * mm, "mid": v(28.87, 26.84) * mm, "end": v(29.17, 27.98) * mm});
            skPoint(sketch, "E27.26.9", {"position": v(28.31, 25.5) * mm});
            skArc(sketch, "E27.26.10", {"start": v(23.34, 26.83) * mm, "mid": v(23.7, 26.7) * mm, "end": v(24.03, 26.85) * mm});
            skArc(sketch, "E27.26.11", {"start": v(26.85, 24.03) * mm, "mid": v(26.7, 23.7) * mm, "end": v(26.83, 23.34) * mm});
            skArc(sketch, "E27.26.12", {"start": v(28.13, 25.3) * mm, "mid": v(28.3, 25.52) * mm, "end": v(28.44, 25.75) * mm});
            skArc(sketch, "E27.26.13", {"start": v(28.43, 29.03) * mm, "mid": v(28.22, 29.16) * mm, "end": v(27.98, 29.17) * mm});
            skArc(sketch, "E27.26.14", {"start": v(29.17, 27.98) * mm, "mid": v(29.16, 28.22) * mm, "end": v(29.03, 28.43) * mm});
            skArc(sketch, "E27.26.15", {"start": v(25.75, 28.44) * mm, "mid": v(25.52, 28.3) * mm, "end": v(25.3, 28.13) * mm});
            skLineSegment(sketch, "E27.26.16", {"start": v(28.43, 29.03) * mm, "end": v(28.73, 28.73) * mm});
            skLineSegment(sketch, "E27.26.17", {"start": v(29.03, 28.43) * mm, "end": v(28.73, 28.73) * mm});
            skPoint(sketch, "E27.27.0", {"position": v(21.55, 34.45) * mm});
            skPoint(sketch, "E27.27.1", {"position": v(19.05, 33) * mm});
            skArc(sketch, "E27.27.2", {"start": v(19.28, 33.17) * mm, "mid": v(20.25, 33.82) * mm, "end": v(21.3, 34.35) * mm});
            skPoint(sketch, "E27.27.3", {"position": v(17.66, 30.86) * mm});
            skPoint(sketch, "E27.27.4", {"position": v(21, 28.7) * mm});
            skLineSegment(sketch, "E27.27.5", {"start": v(18.9, 32.77) * mm, "end": v(17.92, 31.26) * mm});
            skPoint(sketch, "E27.27.6", {"position": v(22.7, 33.7) * mm});
            skLineSegment(sketch, "E27.27.7", {"start": v(22.25, 30.6) * mm, "end": v(21.27, 29.1) * mm});
            skArc(sketch, "E27.27.8", {"start": v(22.46, 31.1) * mm, "mid": v(22.66, 32.26) * mm, "end": v(22.72, 33.43) * mm});
            skPoint(sketch, "E27.27.9", {"position": v(22.4, 30.82) * mm});
            skArc(sketch, "E27.27.10", {"start": v(17.25, 31.1) * mm, "mid": v(17.62, 31.05) * mm, "end": v(17.92, 31.26) * mm});
            skArc(sketch, "E27.27.11", {"start": v(21.27, 29.1) * mm, "mid": v(21.2, 28.73) * mm, "end": v(21.39, 28.4) * mm});
            skArc(sketch, "E27.27.12", {"start": v(22.25, 30.6) * mm, "mid": v(22.38, 30.84) * mm, "end": v(22.46, 31.1) * mm});
            skArc(sketch, "E27.27.13", {"start": v(21.78, 34.3) * mm, "mid": v(21.54, 34.39) * mm, "end": v(21.3, 34.35) * mm});
            skArc(sketch, "E27.27.14", {"start": v(22.72, 33.43) * mm, "mid": v(22.65, 33.67) * mm, "end": v(22.49, 33.85) * mm});
            skArc(sketch, "E27.27.15", {"start": v(19.28, 33.17) * mm, "mid": v(19.07, 33) * mm, "end": v(18.9, 32.77) * mm});
            skLineSegment(sketch, "E27.27.16", {"start": v(21.78, 34.3) * mm, "end": v(22.13, 34.08) * mm});
            skLineSegment(sketch, "E27.27.17", {"start": v(22.49, 33.85) * mm, "end": v(22.13, 34.08) * mm});
            skPoint(sketch, "E27.28.0", {"position": v(13.92, 38.18) * mm});
            skPoint(sketch, "E27.28.1", {"position": v(11.77, 36.24) * mm});
            skArc(sketch, "E27.28.2", {"start": v(11.96, 36.46) * mm, "mid": v(12.78, 37.3) * mm, "end": v(13.7, 38.03) * mm});
            skPoint(sketch, "E27.28.3", {"position": v(10.86, 33.86) * mm});
            skPoint(sketch, "E27.28.4", {"position": v(14.59, 32.43) * mm});
            skLineSegment(sketch, "E27.28.5", {"start": v(11.68, 35.99) * mm, "end": v(11.03, 34.3) * mm});
            skPoint(sketch, "E27.28.6", {"position": v(15.2, 37.69) * mm});
            skLineSegment(sketch, "E27.28.7", {"start": v(15.4, 34.56) * mm, "end": v(14.76, 32.88) * mm});
            skArc(sketch, "E27.28.8", {"start": v(15.5, 35.1) * mm, "mid": v(15.46, 36.27) * mm, "end": v(15.27, 37.42) * mm});
            skPoint(sketch, "E27.28.9", {"position": v(15.5, 34.8) * mm});
            skArc(sketch, "E27.28.10", {"start": v(10.4, 34) * mm, "mid": v(10.78, 34.03) * mm, "end": v(11.03, 34.3) * mm});
            skArc(sketch, "E27.28.11", {"start": v(14.76, 32.88) * mm, "mid": v(14.76, 32.5) * mm, "end": v(15.02, 32.23) * mm});
            skArc(sketch, "E27.28.12", {"start": v(15.4, 34.56) * mm, "mid": v(15.48, 34.82) * mm, "end": v(15.5, 35.1) * mm});
            skArc(sketch, "E27.28.13", {"start": v(14.17, 38.09) * mm, "mid": v(13.92, 38.12) * mm, "end": v(13.7, 38.03) * mm});
            skArc(sketch, "E27.28.14", {"start": v(15.27, 37.42) * mm, "mid": v(15.16, 37.64) * mm, "end": v(14.96, 37.78) * mm});
            skArc(sketch, "E27.28.15", {"start": v(11.96, 36.46) * mm, "mid": v(11.8, 36.24) * mm, "end": v(11.68, 35.99) * mm});
            skLineSegment(sketch, "E27.28.16", {"start": v(14.17, 38.09) * mm, "end": v(14.56, 37.94) * mm});
            skLineSegment(sketch, "E27.28.17", {"start": v(14.96, 37.78) * mm, "end": v(14.56, 37.94) * mm});
            skPoint(sketch, "E27.29.0", {"position": v(5.68, 40.24) * mm});
            skPoint(sketch, "E27.29.1", {"position": v(3.98, 37.9) * mm});
            skArc(sketch, "E27.29.2", {"start": v(4.12, 38.15) * mm, "mid": v(4.74, 39.14) * mm, "end": v(5.49, 40.04) * mm});
            skPoint(sketch, "E27.29.3", {"position": v(3.58, 35.38) * mm});
            skPoint(sketch, "E27.29.4", {"position": v(7.52, 34.76) * mm});
            skLineSegment(sketch, "E27.29.5", {"start": v(3.94, 37.63) * mm, "end": v(3.66, 35.85) * mm});
            skPoint(sketch, "E27.29.6", {"position": v(7.04, 40.03) * mm});
            skLineSegment(sketch, "E27.29.7", {"start": v(7.88, 37) * mm, "end": v(7.6, 35.23) * mm});
            skArc(sketch, "E27.29.8", {"start": v(7.87, 37.55) * mm, "mid": v(7.58, 38.69) * mm, "end": v(7.16, 39.78) * mm});
            skPoint(sketch, "E27.29.9", {"position": v(7.92, 37.27) * mm});
            skArc(sketch, "E27.29.10", {"start": v(3.11, 35.42) * mm, "mid": v(3.47, 35.53) * mm, "end": v(3.66, 35.85) * mm});
            skArc(sketch, "E27.29.11", {"start": v(7.6, 35.23) * mm, "mid": v(7.68, 34.86) * mm, "end": v(7.99, 34.65) * mm});
            skArc(sketch, "E27.29.12", {"start": v(7.88, 37) * mm, "mid": v(7.9, 37.28) * mm, "end": v(7.87, 37.55) * mm});
            skArc(sketch, "E27.29.13", {"start": v(5.94, 40.2) * mm, "mid": v(5.7, 40.18) * mm, "end": v(5.49, 40.04) * mm});
            skArc(sketch, "E27.29.14", {"start": v(7.16, 39.78) * mm, "mid": v(7, 39.97) * mm, "end": v(6.77, 40.07) * mm});
            skArc(sketch, "E27.29.15", {"start": v(4.12, 38.15) * mm, "mid": v(4, 37.9) * mm, "end": v(3.94, 37.63) * mm});
            skLineSegment(sketch, "E27.29.16", {"start": v(5.94, 40.2) * mm, "end": v(6.36, 40.13) * mm});
            skLineSegment(sketch, "E27.29.17", {"start": v(6.77, 40.07) * mm, "end": v(6.36, 40.13) * mm});
            skPoint(sketch, "E27.center", {"position": v(0, 0) * mm});
            skLineSegment(sketch, "E28", {"start": v(0.6, 35.55) * mm, "end": v(3.11, 35.42) * mm});
            skLineSegment(sketch, "E29.1.0", {"start": v(-6.8, 34.9) * mm, "end": v(-4.32, 35.3) * mm});
            skLineSegment(sketch, "E29.2.0", {"start": v(-13.9, 32.73) * mm, "end": v(-11.56, 33.63) * mm});
            skLineSegment(sketch, "E29.3.0", {"start": v(-20.4, 29.12) * mm, "end": v(-18.3, 30.49) * mm});
            skLineSegment(sketch, "E29.4.0", {"start": v(-26.02, 24.24) * mm, "end": v(-24.24, 26.02) * mm});
            skLineSegment(sketch, "E29.5.0", {"start": v(-30.49, 18.3) * mm, "end": v(-29.12, 20.4) * mm});
            skLineSegment(sketch, "E29.6.0", {"start": v(-33.63, 11.56) * mm, "end": v(-32.73, 13.9) * mm});
            skLineSegment(sketch, "E29.7.0", {"start": v(-35.3, 4.32) * mm, "end": v(-34.9, 6.8) * mm});
            skLineSegment(sketch, "E29.8.0", {"start": v(-35.42, -3.11) * mm, "end": v(-35.55, -0.6) * mm});
            skLineSegment(sketch, "E29.9.0", {"start": v(-34, -10.4) * mm, "end": v(-34.65, -7.99) * mm});
            skLineSegment(sketch, "E29.10.0", {"start": v(-31.1, -17.25) * mm, "end": v(-32.23, -15.02) * mm});
            skLineSegment(sketch, "E29.11.0", {"start": v(-26.83, -23.34) * mm, "end": v(-28.4, -21.39) * mm});
            skLineSegment(sketch, "E29.12.0", {"start": v(-21.39, -28.4) * mm, "end": v(-23.34, -26.83) * mm});
            skLineSegment(sketch, "E29.13.0", {"start": v(-15.02, -32.23) * mm, "end": v(-17.25, -31.1) * mm});
            skLineSegment(sketch, "E29.14.0", {"start": v(-7.99, -34.65) * mm, "end": v(-10.4, -34) * mm});
            skLineSegment(sketch, "E29.15.0", {"start": v(-0.6, -35.55) * mm, "end": v(-3.11, -35.42) * mm});
            skLineSegment(sketch, "E29.16.0", {"start": v(6.8, -34.9) * mm, "end": v(4.32, -35.3) * mm});
            skLineSegment(sketch, "E29.17.0", {"start": v(13.9, -32.73) * mm, "end": v(11.56, -33.63) * mm});
            skLineSegment(sketch, "E29.18.0", {"start": v(20.4, -29.12) * mm, "end": v(18.3, -30.49) * mm});
            skLineSegment(sketch, "E29.19.0", {"start": v(26.02, -24.24) * mm, "end": v(24.24, -26.02) * mm});
            skLineSegment(sketch, "E29.20.0", {"start": v(30.49, -18.3) * mm, "end": v(29.12, -20.4) * mm});
            skLineSegment(sketch, "E29.21.0", {"start": v(33.63, -11.56) * mm, "end": v(32.73, -13.9) * mm});
            skLineSegment(sketch, "E29.22.0", {"start": v(35.3, -4.32) * mm, "end": v(34.9, -6.8) * mm});
            skLineSegment(sketch, "E29.23.0", {"start": v(35.42, 3.11) * mm, "end": v(35.55, 0.6) * mm});
            skLineSegment(sketch, "E29.24.0", {"start": v(34, 10.4) * mm, "end": v(34.65, 7.99) * mm});
            skLineSegment(sketch, "E29.25.0", {"start": v(31.1, 17.25) * mm, "end": v(32.23, 15.02) * mm});
            skLineSegment(sketch, "E29.26.0", {"start": v(26.83, 23.34) * mm, "end": v(28.4, 21.39) * mm});
            skLineSegment(sketch, "E29.27.0", {"start": v(21.39, 28.4) * mm, "end": v(23.34, 26.83) * mm});
            skLineSegment(sketch, "E29.28.0", {"start": v(15.02, 32.23) * mm, "end": v(17.25, 31.1) * mm});
            skLineSegment(sketch, "E29.29.0", {"start": v(7.99, 34.65) * mm, "end": v(10.4, 34) * mm});
            skSolve(sketch);
        }
        {
            var Q0;
            Q0=makeQuery(id+"F0.imprint","IMPRINT",FACE,{"disambiguationData":[TD([[makeQuery(id+"F0.imprint","IMPRINT",EDGE,{"derivedFrom":sQuery(id+"F0.wireOp",EDGE,"E0")}),1.0]])]});
            var Q1;
            Q1=makeQuery(id+"F2.imprint","IMPRINT",FACE,{"disambiguationData":[TD([[makeQuery(id+"F2.imprint","IMPRINT",EDGE,{"derivedFrom":sQuery(id+"F2.wireOp",EDGE,"E15")}),1.0]])]});
            var Q2;
            Q2=sQuery(id+"F2.wireOp",VERTEX,"E27.29.11.start");
            var Q3;
            Q3=sQuery(id+"F0.wireOp",VERTEX,"E12.28.2.start");
            loft(context, id + "F3", {"sheetProfilesArray" : [{ "sheetProfileEntities" : qUnion([Q0]) }, { "sheetProfileEntities" : qUnion([Q1]) }], "matchConnections" : true, "connections" : [{ "connectionEntities" : qUnion([Q2, Q3]), "connectionEdgeQueries" : qUnion([]), "connectionEdgeParameters" : [] }]});
        }
        {
            var Q0;
            Q0=makeQuery(id+"F0.imprint","IMPRINT",FACE,{"disambiguationData":[TD([[makeQuery(id+"F0.imprint","IMPRINT",EDGE,{"derivedFrom":sQuery(id+"F0.wireOp",EDGE,"E0")}),1.0]])]});
            var sketch = newSketch(context, id + "F4", { "sketchPlane" : qUnion([Q0])});
            skPoint(sketch, "E30", {"position": v(0, 0) * mm});
            skSolve(sketch);
        }
        {
            var Q0;
            Q0=sQuery(id+"F4.wireOp",VERTEX,"E30");
            var Q1;
            Q1=makeQuery(id+"F3.opLoft","SWEPT_BODY",BODY,{"disambiguationData":[OSD([makeQuery(id+"F0.imprint","IMPRINT",FACE,{"disambiguationData":[TD([[makeQuery(id+"F0.imprint","IMPRINT",EDGE,{"derivedFrom":sQuery(id+"F0.wireOp",EDGE,"E0")}),1.0]])]}),makeQuery(id+"F2.imprint","IMPRINT",FACE,{"disambiguationData":[TD([[makeQuery(id+"F2.imprint","IMPRINT",EDGE,{"derivedFrom":sQuery(id+"F2.wireOp",EDGE,"E15")}),1.0]])]})])]});
            hole(context, id + "F5", {"style" : HoleStyle.SIMPLE, "endStyle" : HoleEndStyle.THROUGH, "holeDiameter" : 12.7 * mm, "tappedDepth" : 12.7 * mm, "tapClearance" : 3, "locations" : qUnion([Q0]), "scope" : qUnion([Q1])});
        }
    });
